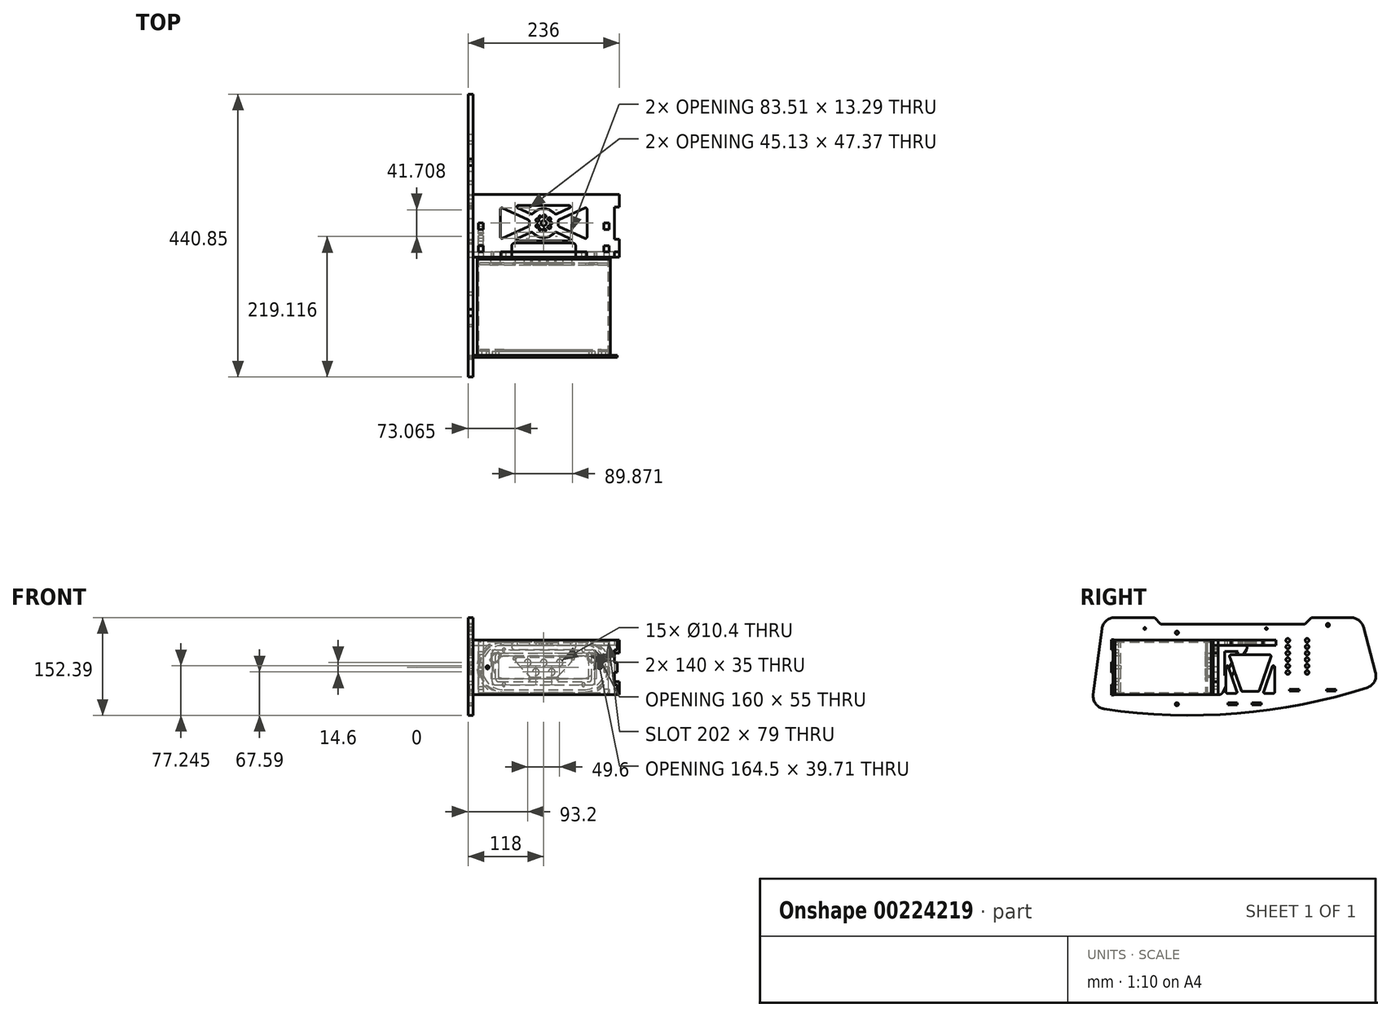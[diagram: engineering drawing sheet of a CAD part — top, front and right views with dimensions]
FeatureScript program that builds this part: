
annotation { "Feature Type Name" : "Feature", "Feature Type Description" : "" }
export const myFeature = defineFeature(function(context is Context, id is Id, definition is map)
    precondition{}
    {
        {
            var Q0;
            Q0=qCreatedBy(makeId("Front.planeOp"),FACE);
            var sketch = newSketch(context, id + "F0", { "sketchPlane" : qUnion([Q0])});
            skLineSegment(sketch, "E0.bottom", {"start": v(-61.5, 42.5) * mm, "end": v(61.5, 42.5) * mm});
            skLineSegment(sketch, "E0.top", {"start": v(-61.5, -42.5) * mm, "end": v(61.5, -42.5) * mm});
            skLineSegment(sketch, "E0.left", {"start": v(-61.5, 42.5) * mm, "end": v(-61.5, -42.5) * mm, "construction": true});
            skLineSegment(sketch, "E0.right", {"start": v(61.5, 42.5) * mm, "end": v(61.5, -42.5) * mm, "construction": true});
            skPoint(sketch, "E0.middle", {"position": v(0, 0) * mm});
            skArc(sketch, "E1", {"start": v(-61.5, 42.5) * mm, "mid": v(-104, 0) * mm, "end": v(-61.5, -42.5) * mm});
            skArc(sketch, "E2", {"start": v(61.5, -42.5) * mm, "mid": v(104, 0) * mm, "end": v(61.5, 42.5) * mm});
            skArc(sketch, "E3.0", {"start": v(61.5, -39.5) * mm, "mid": v(101, 0) * mm, "end": v(61.5, 39.5) * mm});
            skLineSegment(sketch, "E3.1", {"start": v(-61.5, -39.5) * mm, "end": v(61.5, -39.5) * mm});
            skArc(sketch, "E3.2", {"start": v(-61.5, 39.5) * mm, "mid": v(-101, 0) * mm, "end": v(-61.5, -39.5) * mm});
            skLineSegment(sketch, "E3.3", {"start": v(-61.5, 39.5) * mm, "end": v(61.5, 39.5) * mm});
            skSolve(sketch);
        }
        {
            var Q0;
            Q0=makeQuery(id+"F0.imprint","IMPRINT",FACE,{"disambiguationData":[TD([[makeQuery(id+"F0.imprint","IMPRINT",EDGE,{"derivedFrom":sQuery(id+"F0.wireOp",EDGE,"E0.bottom")}),-1.0]])]});
            extrude(context, id + "F1", {"entities" : qUnion([Q0]), "depth" : 150 * mm});
        }
        {
            var Q0;
            Q0=makeQuery(id+"F1.opExtrude","CAP_FACE",FACE,{"disambiguationData":[OSD([sQuery(id+"F0.wireOp",EDGE,"E0.bottom"),sQuery(id+"F0.wireOp",EDGE,"E0.top"),sQuery(id+"F0.wireOp",EDGE,"E1"),sQuery(id+"F0.wireOp",EDGE,"E2"),sQuery(id+"F0.wireOp",EDGE,"E3.0"),sQuery(id+"F0.wireOp",EDGE,"E3.1"),sQuery(id+"F0.wireOp",EDGE,"E3.2"),sQuery(id+"F0.wireOp",EDGE,"E3.3")])],"isStart":true});
            var sketch = newSketch(context, id + "F2", { "sketchPlane" : qUnion([Q0])});
            skArc(sketch, "E4.0", {"start": v(-61.5, -42.5) * mm, "mid": v(-104, 0) * mm, "end": v(-61.5, 42.5) * mm});
            skLineSegment(sketch, "E4.1", {"start": v(61.5, 42.5) * mm, "end": v(-61.5, 42.5) * mm});
            skArc(sketch, "E4.2", {"start": v(61.5, 42.5) * mm, "mid": v(104, 0) * mm, "end": v(61.5, -42.5) * mm});
            skLineSegment(sketch, "E4.3", {"start": v(61.5, -42.5) * mm, "end": v(-61.5, -42.5) * mm});
            skLineSegment(sketch, "E5", {"start": v(0, 23.45) * mm, "end": v(0, 0) * mm, "construction": true});
            skLineSegment(sketch, "E6", {"start": v(-31.44, 0) * mm, "end": v(0, 0) * mm, "construction": true});
            skCircle(sketch, "E7", {"center": v(-62, 27) * mm, "radius": 2.84 * mm});
            skCircle(sketch, "E8.MirrorC", {"center": v(62, 27) * mm, "radius": 2.84 * mm});
            skCircle(sketch, "E9.MirrorC", {"center": v(-62, -27) * mm, "radius": 2.84 * mm});
            skCircle(sketch, "E10.MirrorC", {"center": v(62, -27) * mm, "radius": 2.84 * mm});
            skCircle(sketch, "E11", {"center": v(-24.8, 7.3) * mm, "radius": 5.2 * mm});
            skLineSegment(sketch, "E12.bottom", {"start": v(-30, 12.5) * mm, "end": v(30, 12.5) * mm, "construction": true});
            skLineSegment(sketch, "E12.top", {"start": v(-30, -12.5) * mm, "end": v(30, -12.5) * mm, "construction": true});
            skLineSegment(sketch, "E12.left", {"start": v(-30, 12.5) * mm, "end": v(-30, -12.5) * mm, "construction": true});
            skLineSegment(sketch, "E12.right", {"start": v(30, 12.5) * mm, "end": v(30, -12.5) * mm, "construction": true});
            skPoint(sketch, "E12.middle", {"position": v(0, 0) * mm});
            skCircle(sketch, "E13", {"center": v(0, 7.3) * mm, "radius": 5.2 * mm});
            skCircle(sketch, "E14", {"center": v(24.8, 7.3) * mm, "radius": 5.2 * mm});
            skCircle(sketch, "E15", {"center": v(-12.4, -7.3) * mm, "radius": 5.2 * mm});
            skCircle(sketch, "E16", {"center": v(12.4, -7.3) * mm, "radius": 5.2 * mm});
            skLineSegment(sketch, "E17", {"start": v(-24.8, 7.3) * mm, "end": v(0, 7.3) * mm, "construction": true});
            skLineSegment(sketch, "E18", {"start": v(0, 7.3) * mm, "end": v(24.8, 7.3) * mm, "construction": true});
            skLineSegment(sketch, "E19", {"start": v(-12.4, -7.3) * mm, "end": v(-12.4, 7.3) * mm, "construction": true});
            skLineSegment(sketch, "E20", {"start": v(12.4, -7.3) * mm, "end": v(12.4, 7.3) * mm, "construction": true});
            skCircle(sketch, "E21", {"center": v(-75, 15) * mm, "radius": 7.25 * mm});
            skCircle(sketch, "E22.MirrorC", {"center": v(75, 15) * mm, "radius": 7.25 * mm});
            skSolve(sketch);
        }
        {
            var Q0;
            Q0=makeQuery(id+"F2.imprint","IMPRINT",FACE,{"disambiguationData":[TD([[makeQuery(id+"F2.imprint","IMPRINT",EDGE,{"derivedFrom":sQuery(id+"F2.wireOp",EDGE,"E7")}),-1.0]])]});
            var Q1;
            Q1=makeQuery(id+"F2.imprint","IMPRINT",FACE,{"disambiguationData":[TD([[makeQuery(id+"F2.imprint","IMPRINT",EDGE,{"derivedFrom":sQuery(id+"F2.wireOp",EDGE,"E4.0")}),-1.0]])]});
            extrude(context, id + "F3", {"entities" : qUnion([Q0, Q1]), "depth" : 3 * mm});
        }
        {
            var Q0;
            Q0=makeQuery(id+"F3.opExtrude","CAP_FACE",FACE,{"disambiguationData":[OSD([sQuery(id+"F2.wireOp",EDGE,"E4.0"),sQuery(id+"F2.wireOp",EDGE,"E4.1"),sQuery(id+"F2.wireOp",EDGE,"E4.2"),sQuery(id+"F2.wireOp",EDGE,"E4.3"),sQuery(id+"F2.wireOp",EDGE,"E7"),sQuery(id+"F2.wireOp",EDGE,"E8.MirrorC"),sQuery(id+"F2.wireOp",EDGE,"E9.MirrorC"),sQuery(id+"F2.wireOp",EDGE,"E10.MirrorC"),sQuery(id+"F2.wireOp",EDGE,"E11"),sQuery(id+"F2.wireOp",EDGE,"E13"),sQuery(id+"F2.wireOp",EDGE,"E14"),sQuery(id+"F2.wireOp",EDGE,"E15"),sQuery(id+"F2.wireOp",EDGE,"E16"),sQuery(id+"F2.wireOp",EDGE,"E21"),sQuery(id+"F2.wireOp",EDGE,"E22.MirrorC")])],"isStart":true});
            var sketch = newSketch(context, id + "F4", { "sketchPlane" : qUnion([Q0])});
            skCircle(sketch, "E23.0", {"center": v(-75, 15) * mm, "radius": 7.25 * mm});
            skCircle(sketch, "E23.1", {"center": v(-62, 27) * mm, "radius": 2.84 * mm});
            skCircle(sketch, "E23.2", {"center": v(-62, -27) * mm, "radius": 2.84 * mm});
            skCircle(sketch, "E23.3", {"center": v(62, -27) * mm, "radius": 2.84 * mm});
            skCircle(sketch, "E23.4", {"center": v(62, 27) * mm, "radius": 2.84 * mm});
            skCircle(sketch, "E23.5", {"center": v(75, 15) * mm, "radius": 7.25 * mm});
            skLineSegment(sketch, "E24.0", {"start": v(-61.5, 39.5) * mm, "end": v(61.5, 39.5) * mm});
            skArc(sketch, "E24.1", {"start": v(-61.5, 39.5) * mm, "mid": v(-101, 0) * mm, "end": v(-61.5, -39.5) * mm});
            skLineSegment(sketch, "E24.2", {"start": v(-61.5, -39.5) * mm, "end": v(61.5, -39.5) * mm});
            skArc(sketch, "E24.3", {"start": v(61.5, -39.5) * mm, "mid": v(101, 0) * mm, "end": v(61.5, 39.5) * mm});
            skArc(sketch, "E25.0", {"start": v(-61.5, 35.05) * mm, "mid": v(-96.55, 0) * mm, "end": v(-61.5, -35.05) * mm});
            skLineSegment(sketch, "E25.1", {"start": v(-61.5, 35.05) * mm, "end": v(61.5, 35.05) * mm});
            skArc(sketch, "E25.2", {"start": v(61.5, -35.05) * mm, "mid": v(96.55, 0) * mm, "end": v(61.5, 35.05) * mm});
            skLineSegment(sketch, "E25.3", {"start": v(-61.5, -35.05) * mm, "end": v(61.5, -35.05) * mm});
            skLineSegment(sketch, "E26", {"start": v(-46.82, 4.18) * mm, "end": v(-26.32, -17.82) * mm});
            skLineSegment(sketch, "E27", {"start": v(-19, -21) * mm, "end": v(19, -21) * mm});
            skLineSegment(sketch, "E28", {"start": v(26.32, -17.82) * mm, "end": v(46.82, 4.18) * mm});
            skLineSegment(sketch, "E29", {"start": v(39.5, 21) * mm, "end": v(-39.5, 21) * mm});
            skLineSegment(sketch, "E30", {"start": v(0, 21) * mm, "end": v(0, -21) * mm});
            skPoint(sketch, "E31.visualSharp", {"position": v(-62.49, 21) * mm});
            skArc(sketch, "E31.filletArc", {"start": v(-39.5, 21) * mm, "mid": v(-48.67, 14.99) * mm, "end": v(-46.82, 4.18) * mm});
            skPoint(sketch, "E32.visualSharp", {"position": v(-23.35, -21) * mm});
            skArc(sketch, "E32.filletArc", {"start": v(-26.32, -17.82) * mm, "mid": v(-22.99, -20.17) * mm, "end": v(-19, -21) * mm});
            skPoint(sketch, "E33.visualSharp", {"position": v(23.35, -21) * mm});
            skArc(sketch, "E33.filletArc", {"start": v(19, -21) * mm, "mid": v(22.99, -20.17) * mm, "end": v(26.32, -17.82) * mm});
            skPoint(sketch, "E34.visualSharp", {"position": v(62.49, 21) * mm});
            skArc(sketch, "E34.filletArc", {"start": v(46.82, 4.18) * mm, "mid": v(48.67, 14.99) * mm, "end": v(39.5, 21) * mm});
            skSolve(sketch);
        }
        {
            var Q0;
            Q0=makeQuery(id+"F4.imprint","IMPRINT",FACE,{"disambiguationData":[TD([[makeQuery(id+"F4.imprint","IMPRINT",EDGE,{"derivedFrom":sQuery(id+"F4.wireOp",EDGE,"E23.0")}),-1.0]])]});
            extrude(context, id + "F5", {"entities" : qUnion([Q0]), "depth" : 6 * mm});
        }
        {
            var Q0;
            Q0=makeQuery(id+"F3.opExtrude","CAP_FACE",FACE,{"disambiguationData":[OSD([sQuery(id+"F2.wireOp",EDGE,"E4.0"),sQuery(id+"F2.wireOp",EDGE,"E4.1"),sQuery(id+"F2.wireOp",EDGE,"E4.2"),sQuery(id+"F2.wireOp",EDGE,"E4.3"),sQuery(id+"F2.wireOp",EDGE,"E7"),sQuery(id+"F2.wireOp",EDGE,"E8.MirrorC"),sQuery(id+"F2.wireOp",EDGE,"E9.MirrorC"),sQuery(id+"F2.wireOp",EDGE,"E10.MirrorC"),sQuery(id+"F2.wireOp",EDGE,"E11"),sQuery(id+"F2.wireOp",EDGE,"E13"),sQuery(id+"F2.wireOp",EDGE,"E14"),sQuery(id+"F2.wireOp",EDGE,"E15"),sQuery(id+"F2.wireOp",EDGE,"E16"),sQuery(id+"F2.wireOp",EDGE,"E21"),sQuery(id+"F2.wireOp",EDGE,"E22.MirrorC")])],"isStart":true});
            var sketch = newSketch(context, id + "F6", { "sketchPlane" : qUnion([Q0])});
            skCircle(sketch, "E35.0", {"center": v(-24.8, 7.3) * mm, "radius": 5.2 * mm});
            skCircle(sketch, "E35.1", {"center": v(0, 7.3) * mm, "radius": 5.2 * mm});
            skCircle(sketch, "E35.2", {"center": v(24.8, 7.3) * mm, "radius": 5.2 * mm});
            skCircle(sketch, "E35.3", {"center": v(12.4, -7.3) * mm, "radius": 5.2 * mm});
            skCircle(sketch, "E35.4", {"center": v(-12.4, -7.3) * mm, "radius": 5.2 * mm});
            skLineSegment(sketch, "E36.0", {"start": v(39.5, 21) * mm, "end": v(-39.5, 21) * mm});
            skArc(sketch, "E36.1", {"start": v(-39.5, 21) * mm, "mid": v(-48.67, 14.99) * mm, "end": v(-46.82, 4.18) * mm});
            skLineSegment(sketch, "E36.2", {"start": v(-46.82, 4.18) * mm, "end": v(-26.32, -17.82) * mm});
            skArc(sketch, "E36.3", {"start": v(-26.32, -17.82) * mm, "mid": v(-22.99, -20.17) * mm, "end": v(-19, -21) * mm});
            skLineSegment(sketch, "E36.4", {"start": v(-19, -21) * mm, "end": v(19, -21) * mm});
            skArc(sketch, "E36.5", {"start": v(19, -21) * mm, "mid": v(22.99, -20.17) * mm, "end": v(26.32, -17.82) * mm});
            skLineSegment(sketch, "E36.6", {"start": v(26.32, -17.82) * mm, "end": v(46.82, 4.18) * mm});
            skArc(sketch, "E36.7", {"start": v(46.82, 4.18) * mm, "mid": v(48.67, 14.99) * mm, "end": v(39.5, 21) * mm});
            skLineSegment(sketch, "E37.0", {"start": v(39.5, 15.5) * mm, "end": v(-39.5, 15.5) * mm});
            skArc(sketch, "E37.1", {"start": v(42.8, 7.93) * mm, "mid": v(43.63, 12.8) * mm, "end": v(39.5, 15.5) * mm});
            skArc(sketch, "E37.2", {"start": v(-39.5, 15.5) * mm, "mid": v(-43.63, 12.8) * mm, "end": v(-42.8, 7.93) * mm});
            skLineSegment(sketch, "E37.3", {"start": v(22.3, -14.07) * mm, "end": v(42.8, 7.93) * mm});
            skLineSegment(sketch, "E37.4", {"start": v(-42.8, 7.93) * mm, "end": v(-22.3, -14.07) * mm});
            skArc(sketch, "E37.5", {"start": v(-22.3, -14.07) * mm, "mid": v(-20.8, -15.13) * mm, "end": v(-19, -15.5) * mm});
            skLineSegment(sketch, "E37.6", {"start": v(-19, -15.5) * mm, "end": v(19, -15.5) * mm});
            skArc(sketch, "E37.7", {"start": v(19, -15.5) * mm, "mid": v(20.8, -15.13) * mm, "end": v(22.3, -14.07) * mm});
            skSolve(sketch);
        }
        {
            var Q0;
            Q0=makeQuery(id+"F6.imprint","IMPRINT",FACE,{"disambiguationData":[TD([[makeQuery(id+"F6.imprint","IMPRINT",EDGE,{"derivedFrom":sQuery(id+"F6.wireOp",EDGE,"E35.0")}),1.0]])]});
            extrude(context, id + "F7", {"entities" : qUnion([Q0]), "depth" : 6 * mm});
        }
        {
            var Q0;
            Q0=makeQuery(id+"F5.opExtrude","CAP_FACE",FACE,{"disambiguationData":[OSD([sQuery(id+"F4.wireOp",EDGE,"E23.0"),sQuery(id+"F4.wireOp",EDGE,"E23.1"),sQuery(id+"F4.wireOp",EDGE,"E23.2"),sQuery(id+"F4.wireOp",EDGE,"E23.3"),sQuery(id+"F4.wireOp",EDGE,"E23.4"),sQuery(id+"F4.wireOp",EDGE,"E23.5"),sQuery(id+"F4.wireOp",EDGE,"E25.0"),sQuery(id+"F4.wireOp",EDGE,"E25.1"),sQuery(id+"F4.wireOp",EDGE,"E25.2"),sQuery(id+"F4.wireOp",EDGE,"E25.3"),sQuery(id+"F4.wireOp",EDGE,"E26"),sQuery(id+"F4.wireOp",EDGE,"E27"),sQuery(id+"F4.wireOp",EDGE,"E28"),sQuery(id+"F4.wireOp",EDGE,"E29"),sQuery(id+"F4.wireOp",EDGE,"E31.filletArc"),sQuery(id+"F4.wireOp",EDGE,"E32.filletArc"),sQuery(id+"F4.wireOp",EDGE,"E33.filletArc"),sQuery(id+"F4.wireOp",EDGE,"E34.filletArc")])],"isStart":false});
            var sketch = newSketch(context, id + "F8", { "sketchPlane" : qUnion([Q0])});
            skArc(sketch, "E38.0", {"start": v(-61.5, 38.5) * mm, "mid": v(-100, 0) * mm, "end": v(-61.5, -38.5) * mm});
            skLineSegment(sketch, "E38.1", {"start": v(-61.5, 38.5) * mm, "end": v(61.5, 38.5) * mm});
            skArc(sketch, "E38.2", {"start": v(61.5, -38.5) * mm, "mid": v(100, 0) * mm, "end": v(61.5, 38.5) * mm});
            skLineSegment(sketch, "E38.3", {"start": v(-61.5, -38.5) * mm, "end": v(61.5, -38.5) * mm});
            skCircle(sketch, "E39.0", {"center": v(-24.8, 7.3) * mm, "radius": 5.2 * mm});
            skCircle(sketch, "E39.1", {"center": v(0, 7.3) * mm, "radius": 5.2 * mm});
            skCircle(sketch, "E39.2", {"center": v(24.8, 7.3) * mm, "radius": 5.2 * mm});
            skCircle(sketch, "E39.3", {"center": v(12.4, -7.3) * mm, "radius": 5.2 * mm});
            skCircle(sketch, "E39.4", {"center": v(-12.4, -7.3) * mm, "radius": 5.2 * mm});
            skPoint(sketch, "E40", {"position": v(-75, 15) * mm});
            skLineSegment(sketch, "E41", {"start": v(-71.82, 25.25) * mm, "end": v(-85.25, 11.82) * mm});
            skLineSegment(sketch, "E42", {"start": v(-85.25, 11.82) * mm, "end": v(-78.18, 4.75) * mm});
            skLineSegment(sketch, "E43", {"start": v(-78.18, 4.75) * mm, "end": v(-64.75, 18.18) * mm});
            skLineSegment(sketch, "E44", {"start": v(-64.75, 18.18) * mm, "end": v(-71.82, 25.25) * mm});
            skLineSegment(sketch, "E45", {"start": v(-85.25, 11.82) * mm, "end": v(-85.25, 27.38) * mm});
            skLineSegment(sketch, "E46", {"start": v(-71.82, 25.25) * mm, "end": v(-78.18, 4.75) * mm, "construction": true});
            skCircle(sketch, "E47", {"center": v(-75, 15) * mm, "radius": 5.25 * mm});
            skLineSegment(sketch, "E48", {"start": v(-68.28, 21.72) * mm, "end": v(-81.72, 8.28) * mm, "construction": true});
            skLineSegment(sketch, "E49", {"start": v(-78.54, 18.54) * mm, "end": v(-71.46, 11.46) * mm, "construction": true});
            skLineSegment(sketch, "E50", {"start": v(-70.86, 24.3) * mm, "end": v(-78, 19.3) * mm});
            skLineSegment(sketch, "E51.MirrorCS", {"start": v(-65.7, 19.14) * mm, "end": v(-70.7, 12) * mm});
            skLineSegment(sketch, "E52.MirrorCS", {"start": v(-84.3, 10.86) * mm, "end": v(-79.3, 18) * mm});
            skLineSegment(sketch, "E53.MirrorCS", {"start": v(-79.14, 5.7) * mm, "end": v(-72, 10.7) * mm});
            skLineSegment(sketch, "E54", {"start": v(0, -1.17) * mm, "end": v(0, 25.72) * mm, "construction": true});
            skPoint(sketch, "E54.endSnap0", {"position": v(0, 21) * mm});
            skLineSegment(sketch, "E55.MirrorCS", {"start": v(78.54, 18.54) * mm, "end": v(71.46, 11.46) * mm, "construction": true});
            skLineSegment(sketch, "E56.MirrorCS", {"start": v(85.25, 11.82) * mm, "end": v(78.18, 4.75) * mm});
            skLineSegment(sketch, "E57.MirrorCS", {"start": v(64.75, 18.18) * mm, "end": v(71.82, 25.25) * mm});
            skArc(sketch, "E58.MirrorCS", {"start": v(61.5, 38.5) * mm, "mid": v(100, 0) * mm, "end": v(61.5, -38.5) * mm});
            skLineSegment(sketch, "E59.MirrorCS", {"start": v(84.3, 10.86) * mm, "end": v(79.3, 18) * mm});
            skCircle(sketch, "E60.MirrorC", {"center": v(75, 15) * mm, "radius": 5.25 * mm});
            skLineSegment(sketch, "E61.MirrorCS", {"start": v(71.82, 25.25) * mm, "end": v(78.18, 4.75) * mm, "construction": true});
            skLineSegment(sketch, "E62.MirrorCS", {"start": v(71.82, 25.25) * mm, "end": v(85.25, 11.82) * mm});
            skLineSegment(sketch, "E63.MirrorCS", {"start": v(70.86, 24.3) * mm, "end": v(78, 19.3) * mm});
            skLineSegment(sketch, "E64.MirrorCS", {"start": v(85.25, 11.82) * mm, "end": v(85.25, 27.38) * mm});
            skLineSegment(sketch, "E65.MirrorCS", {"start": v(68.28, 21.72) * mm, "end": v(81.72, 8.28) * mm, "construction": true});
            skLineSegment(sketch, "E66.MirrorCS", {"start": v(65.7, 19.14) * mm, "end": v(70.7, 12) * mm});
            skLineSegment(sketch, "E67.MirrorCS", {"start": v(79.14, 5.7) * mm, "end": v(72, 10.7) * mm});
            skLineSegment(sketch, "E68.MirrorCS", {"start": v(78.18, 4.75) * mm, "end": v(64.75, 18.18) * mm});
            skPoint(sketch, "E69", {"position": v(-48.67, 14.99) * mm});
            skPoint(sketch, "E70.0", {"position": v(-43.63, 12.8) * mm});
            skLineSegment(sketch, "E71", {"start": v(-48.67, 14.99) * mm, "end": v(-43.63, 12.8) * mm, "construction": true});
            skCircle(sketch, "E72", {"center": v(-46.15, 13.9) * mm, "radius": 2 * mm});
            skLineSegment(sketch, "E73", {"start": v(-22.99, -20.17) * mm, "end": v(-20.8, -15.13) * mm, "construction": true});
            skCircle(sketch, "E74", {"center": v(-21.9, -17.65) * mm, "radius": 2 * mm});
            skCircle(sketch, "E75.MirrorC", {"center": v(46.15, 13.9) * mm, "radius": 2 * mm});
            skCircle(sketch, "E76.MirrorC", {"center": v(21.9, -17.65) * mm, "radius": 2 * mm});
            skSolve(sketch);
        }
        {
            var Q0;
            Q0=makeQuery(id+"F8.imprint","IMPRINT",FACE,{"disambiguationData":[TD([[makeQuery(id+"F8.imprint","IMPRINT",EDGE,{"derivedFrom":makeQuery(id+"F5.opExtrude","CAP_EDGE",EDGE,{"disambiguationData":[OSD([sQuery(id+"F4.wireOp",EDGE,"E23.1")])],"isStart":false})}),1.0]])]});
            var Q1;
            Q1=makeQuery(id+"F8.imprint","IMPRINT",FACE,{"disambiguationData":[TD([[makeQuery(id+"F8.imprint","IMPRINT",EDGE,{"derivedFrom":makeQuery(id+"F5.opExtrude","CAP_EDGE",EDGE,{"disambiguationData":[OSD([sQuery(id+"F4.wireOp",EDGE,"E23.2")])],"isStart":false})}),-1.0]])]});
            var Q2;
            Q2=makeQuery(id+"F8.imprint","IMPRINT",FACE,{"disambiguationData":[TD([[makeQuery(id+"F8.imprint","IMPRINT",EDGE,{"derivedFrom":makeQuery(id+"F5.opExtrude","CAP_EDGE",EDGE,{"disambiguationData":[OSD([sQuery(id+"F4.wireOp",EDGE,"E23.3")])],"isStart":false})}),1.0]])]});
            var Q3;
            Q3=makeQuery(id+"F8.imprint","IMPRINT",FACE,{"disambiguationData":[TD([[makeQuery(id+"F8.imprint","IMPRINT",EDGE,{"derivedFrom":makeQuery(id+"F5.opExtrude","CAP_EDGE",EDGE,{"disambiguationData":[OSD([sQuery(id+"F4.wireOp",EDGE,"E23.4")])],"isStart":false})}),-1.0]])]});
            var Q4;
            Q4=makeQuery(id+"F8.imprint","IMPRINT",FACE,{"disambiguationData":[TD([[makeQuery(id+"F8.imprint","IMPRINT",EDGE,{"derivedFrom":sQuery(id+"F8.wireOp",EDGE,"E39.0")}),-1.0]])]});
            var Q5;
            {var subQ0=sQuery(id+"F8.wireOp",EDGE,"E50");var subQ3=sQuery(id+"F8.wireOp",EDGE,"E41");var subQ4=makeQuery(id+"F8.imprint","INTERSECT",VERTEX,{"derivedFrom":[subQ3,subQ0]});Q5=makeQuery(id+"F8.imprint","IMPRINT",FACE,{"disambiguationData":[TD([[makeQuery(id+"F8.imprint","IMPRINT",EDGE,{"disambiguationData":[TD([[subQ4,1.0]])],"derivedFrom":subQ3}),-1.0]])]});}
            var Q6;
            {var subQ1=sQuery(id+"F8.wireOp",EDGE,"E59.MirrorCS");var subQ8=sQuery(id+"F8.wireOp",EDGE,"E60.MirrorC");var subQ9=makeQuery(id+"F8.imprint","INTERSECT",VERTEX,{"derivedFrom":[subQ1,subQ8]});Q6=makeQuery(id+"F8.imprint","IMPRINT",FACE,{"disambiguationData":[TD([[makeQuery(id+"F8.imprint","IMPRINT",EDGE,{"disambiguationData":[TD([[subQ9,1.0]])],"derivedFrom":subQ1}),-1.0]])]});}
            var Q7;
            {var subQ5=sQuery(id+"F8.wireOp",EDGE,"E60.MirrorC");var subQ7=sQuery(id+"F8.wireOp",EDGE,"E66.MirrorCS");var subQ8=makeQuery(id+"F8.imprint","INTERSECT",VERTEX,{"derivedFrom":[subQ5,subQ7]});Q7=makeQuery(id+"F8.imprint","IMPRINT",FACE,{"disambiguationData":[TD([[makeQuery(id+"F8.imprint","IMPRINT",EDGE,{"disambiguationData":[TD([[subQ8,1.0]])],"derivedFrom":subQ5}),1.0]])]});}
            var Q8;
            Q8=makeQuery(id+"F8.imprint","IMPRINT",FACE,{"disambiguationData":[TD([[makeQuery(id+"F8.imprint","IMPRINT",EDGE,{"derivedFrom":sQuery(id+"F8.wireOp",EDGE,"E38.0")}),1.0]])]});
            var Q9;
            Q9=makeQuery(id+"F8.imprint","IMPRINT",FACE,{"disambiguationData":[TD([[makeQuery(id+"F8.imprint","IMPRINT",EDGE,{"derivedFrom":makeQuery(id+"F5.opExtrude","CAP_EDGE",EDGE,{"disambiguationData":[OSD([sQuery(id+"F4.wireOp",EDGE,"E23.1")])],"isStart":false})}),-1.0]])]});
            var Q10;
            {var subQ0=sQuery(id+"F8.wireOp",EDGE,"E43");var subQ1=sQuery(id+"F8.wireOp",EDGE,"E42");var subQ2=makeQuery(id+"F8.imprint","INTERSECT",VERTEX,{"derivedFrom":[subQ1,subQ0]});Q10=makeQuery(id+"F8.imprint","IMPRINT",FACE,{"disambiguationData":[TD([[makeQuery(id+"F8.imprint","IMPRINT",EDGE,{"disambiguationData":[TD([[subQ2,1.0]])],"derivedFrom":subQ1}),1.0]])]});}
            var Q11;
            {var subQ0=sQuery(id+"F8.wireOp",EDGE,"E53.MirrorCS");var subQ1=sQuery(id+"F8.wireOp",EDGE,"E43");var subQ2=makeQuery(id+"F8.imprint","INTERSECT",VERTEX,{"derivedFrom":[subQ1,subQ0]});Q11=makeQuery(id+"F8.imprint","IMPRINT",FACE,{"disambiguationData":[TD([[makeQuery(id+"F8.imprint","IMPRINT",EDGE,{"disambiguationData":[TD([[subQ2,1.0]])],"derivedFrom":subQ1}),1.0]])]});}
            var Q12;
            {var subQ3=sQuery(id+"F8.wireOp",EDGE,"E43");var subQ8=sQuery(id+"F8.wireOp",EDGE,"E53.MirrorCS");var subQ10=makeQuery(id+"F8.imprint","INTERSECT",VERTEX,{"derivedFrom":[subQ3,subQ8]});Q12=makeQuery(id+"F8.imprint","IMPRINT",FACE,{"disambiguationData":[TD([[makeQuery(id+"F8.imprint","IMPRINT",EDGE,{"disambiguationData":[TD([[subQ10,1.0]])],"derivedFrom":subQ3}),-1.0]])]});}
            var Q13;
            {var subQ0=sQuery(id+"F8.wireOp",EDGE,"E51.MirrorCS");var subQ1=sQuery(id+"F8.wireOp",EDGE,"E43");var subQ2=makeQuery(id+"F8.imprint","INTERSECT",VERTEX,{"derivedFrom":[subQ1,subQ0]});Q13=makeQuery(id+"F8.imprint","IMPRINT",FACE,{"disambiguationData":[TD([[makeQuery(id+"F8.imprint","IMPRINT",EDGE,{"disambiguationData":[TD([[subQ2,-1.0]])],"derivedFrom":subQ1}),1.0]])]});}
            var Q14;
            {var subQ0=sQuery(id+"F8.wireOp",EDGE,"E44");var subQ1=sQuery(id+"F8.wireOp",EDGE,"E43");var subQ2=makeQuery(id+"F8.imprint","INTERSECT",VERTEX,{"derivedFrom":[subQ1,subQ0]});Q14=makeQuery(id+"F8.imprint","IMPRINT",FACE,{"disambiguationData":[TD([[makeQuery(id+"F8.imprint","IMPRINT",EDGE,{"disambiguationData":[TD([[subQ2,1.0]])],"derivedFrom":subQ1}),1.0]])]});}
            var Q15;
            {var subQ0=sQuery(id+"F8.wireOp",EDGE,"E44");var subQ1=sQuery(id+"F8.wireOp",EDGE,"E41");var subQ2=makeQuery(id+"F8.imprint","INTERSECT",VERTEX,{"derivedFrom":[subQ1,subQ0]});Q15=makeQuery(id+"F8.imprint","IMPRINT",FACE,{"disambiguationData":[TD([[makeQuery(id+"F8.imprint","IMPRINT",EDGE,{"disambiguationData":[TD([[subQ2,-1.0]])],"derivedFrom":subQ1}),1.0]])]});}
            var Q16;
            {var subQ0=sQuery(id+"F8.wireOp",EDGE,"E50");var subQ1=sQuery(id+"F8.wireOp",EDGE,"E41");var subQ2=makeQuery(id+"F8.imprint","INTERSECT",VERTEX,{"derivedFrom":[subQ1,subQ0]});Q16=makeQuery(id+"F8.imprint","IMPRINT",FACE,{"disambiguationData":[TD([[makeQuery(id+"F8.imprint","IMPRINT",EDGE,{"disambiguationData":[TD([[subQ2,1.0]])],"derivedFrom":subQ1}),1.0]])]});}
            var Q17;
            {var subQ0=sQuery(id+"F8.wireOp",EDGE,"E52.MirrorCS");var subQ1=sQuery(id+"F8.wireOp",EDGE,"E41");var subQ2=makeQuery(id+"F8.imprint","INTERSECT",VERTEX,{"derivedFrom":[subQ1,subQ0]});Q17=makeQuery(id+"F8.imprint","IMPRINT",FACE,{"disambiguationData":[TD([[makeQuery(id+"F8.imprint","IMPRINT",EDGE,{"disambiguationData":[TD([[subQ2,-1.0]])],"derivedFrom":subQ1}),1.0]])]});}
            var Q18;
            {var subQ0=sQuery(id+"F8.wireOp",EDGE,"E42");var subQ1=sQuery(id+"F8.wireOp",EDGE,"E41");var subQ2=makeQuery(id+"F8.imprint","INTERSECT",VERTEX,{"derivedFrom":[subQ1,subQ0]});Q18=makeQuery(id+"F8.imprint","IMPRINT",FACE,{"disambiguationData":[TD([[makeQuery(id+"F8.imprint","IMPRINT",EDGE,{"disambiguationData":[TD([[subQ2,1.0]])],"derivedFrom":subQ1}),1.0]])]});}
            var Q19;
            {var subQ0=sQuery(id+"F8.wireOp",EDGE,"E68.MirrorCS");var subQ1=sQuery(id+"F8.wireOp",EDGE,"E57.MirrorCS");var subQ2=makeQuery(id+"F8.imprint","INTERSECT",VERTEX,{"derivedFrom":[subQ1,subQ0]});Q19=makeQuery(id+"F8.imprint","IMPRINT",FACE,{"disambiguationData":[TD([[makeQuery(id+"F8.imprint","IMPRINT",EDGE,{"disambiguationData":[TD([[subQ2,-1.0]])],"derivedFrom":subQ1}),-1.0]])]});}
            var Q20;
            {var subQ0=sQuery(id+"F8.wireOp",EDGE,"E68.MirrorCS");var subQ1=sQuery(id+"F8.wireOp",EDGE,"E66.MirrorCS");var subQ2=makeQuery(id+"F8.imprint","INTERSECT",VERTEX,{"derivedFrom":[subQ1,subQ0]});Q20=makeQuery(id+"F8.imprint","IMPRINT",FACE,{"disambiguationData":[TD([[makeQuery(id+"F8.imprint","IMPRINT",EDGE,{"disambiguationData":[TD([[subQ2,1.0]])],"derivedFrom":subQ1}),-1.0]])]});}
            var Q21;
            {var subQ0=sQuery(id+"F8.wireOp",EDGE,"E68.MirrorCS");var subQ1=sQuery(id+"F8.wireOp",EDGE,"E67.MirrorCS");var subQ2=makeQuery(id+"F8.imprint","INTERSECT",VERTEX,{"derivedFrom":[subQ1,subQ0]});Q21=makeQuery(id+"F8.imprint","IMPRINT",FACE,{"disambiguationData":[TD([[makeQuery(id+"F8.imprint","IMPRINT",EDGE,{"disambiguationData":[TD([[subQ2,1.0]])],"derivedFrom":subQ1}),1.0]])]});}
            var Q22;
            {var subQ0=sQuery(id+"F8.wireOp",EDGE,"E68.MirrorCS");var subQ1=sQuery(id+"F8.wireOp",EDGE,"E56.MirrorCS");var subQ2=makeQuery(id+"F8.imprint","INTERSECT",VERTEX,{"derivedFrom":[subQ1,subQ0]});Q22=makeQuery(id+"F8.imprint","IMPRINT",FACE,{"disambiguationData":[TD([[makeQuery(id+"F8.imprint","IMPRINT",EDGE,{"disambiguationData":[TD([[subQ2,1.0]])],"derivedFrom":subQ1}),-1.0]])]});}
            var Q23;
            {var subQ0=sQuery(id+"F8.wireOp",EDGE,"E62.MirrorCS");var subQ1=sQuery(id+"F8.wireOp",EDGE,"E57.MirrorCS");var subQ2=makeQuery(id+"F8.imprint","INTERSECT",VERTEX,{"derivedFrom":[subQ1,subQ0]});Q23=makeQuery(id+"F8.imprint","IMPRINT",FACE,{"disambiguationData":[TD([[makeQuery(id+"F8.imprint","IMPRINT",EDGE,{"disambiguationData":[TD([[subQ2,1.0]])],"derivedFrom":subQ1}),-1.0]])]});}
            var Q24;
            {var subQ0=sQuery(id+"F8.wireOp",EDGE,"E63.MirrorCS");var subQ1=sQuery(id+"F8.wireOp",EDGE,"E62.MirrorCS");var subQ2=makeQuery(id+"F8.imprint","INTERSECT",VERTEX,{"derivedFrom":[subQ1,subQ0]});Q24=makeQuery(id+"F8.imprint","IMPRINT",FACE,{"disambiguationData":[TD([[makeQuery(id+"F8.imprint","IMPRINT",EDGE,{"disambiguationData":[TD([[subQ2,1.0]])],"derivedFrom":subQ1}),-1.0]])]});}
            var Q25;
            {var subQ0=sQuery(id+"F8.wireOp",EDGE,"E62.MirrorCS");var subQ1=sQuery(id+"F8.wireOp",EDGE,"E59.MirrorCS");var subQ2=makeQuery(id+"F8.imprint","INTERSECT",VERTEX,{"derivedFrom":[subQ1,subQ0]});Q25=makeQuery(id+"F8.imprint","IMPRINT",FACE,{"disambiguationData":[TD([[makeQuery(id+"F8.imprint","IMPRINT",EDGE,{"disambiguationData":[TD([[subQ2,1.0]])],"derivedFrom":subQ1}),-1.0]])]});}
            var Q26;
            {var subQ0=sQuery(id+"F8.wireOp",EDGE,"E62.MirrorCS");var subQ1=sQuery(id+"F8.wireOp",EDGE,"E56.MirrorCS");var subQ2=makeQuery(id+"F8.imprint","INTERSECT",VERTEX,{"derivedFrom":[subQ1,subQ0]});Q26=makeQuery(id+"F8.imprint","IMPRINT",FACE,{"disambiguationData":[TD([[makeQuery(id+"F8.imprint","IMPRINT",EDGE,{"disambiguationData":[TD([[subQ2,-1.0]])],"derivedFrom":subQ1}),-1.0]])]});}
            extrude(context, id + "F9", {"entities" : qUnion([Q0, Q1, Q2, Q3, Q4, Q5, Q6, Q7, Q8, Q9, Q10, Q11, Q12, Q13, Q14, Q15, Q16, Q17, Q18, Q19, Q20, Q21, Q22, Q23, Q24, Q25, Q26]), "depth" : 3 * mm});
        }
        {
            var Q0;
            Q0=makeQuery(id+"F3.opExtrude","CAP_FACE",FACE,{"disambiguationData":[OSD([sQuery(id+"F2.wireOp",EDGE,"E4.0"),sQuery(id+"F2.wireOp",EDGE,"E4.1"),sQuery(id+"F2.wireOp",EDGE,"E4.2"),sQuery(id+"F2.wireOp",EDGE,"E4.3"),sQuery(id+"F2.wireOp",EDGE,"E7"),sQuery(id+"F2.wireOp",EDGE,"E8.MirrorC"),sQuery(id+"F2.wireOp",EDGE,"E9.MirrorC"),sQuery(id+"F2.wireOp",EDGE,"E10.MirrorC"),sQuery(id+"F2.wireOp",EDGE,"E11"),sQuery(id+"F2.wireOp",EDGE,"E13"),sQuery(id+"F2.wireOp",EDGE,"E14"),sQuery(id+"F2.wireOp",EDGE,"E15"),sQuery(id+"F2.wireOp",EDGE,"E16"),sQuery(id+"F2.wireOp",EDGE,"E21"),sQuery(id+"F2.wireOp",EDGE,"E22.MirrorC")])],"isStart":false});
            var sketch = newSketch(context, id + "F10", { "sketchPlane" : qUnion([Q0])});
            skLineSegment(sketch, "E77.bottom", {"start": v(110, 42.5) * mm, "end": v(-110, 42.5) * mm});
            skLineSegment(sketch, "E77.top", {"start": v(110, -42.5) * mm, "end": v(-110, -42.5) * mm});
            skLineSegment(sketch, "E77.left", {"start": v(110, 42.5) * mm, "end": v(110, -42.5) * mm});
            skLineSegment(sketch, "E77.right", {"start": v(-110, 42.5) * mm, "end": v(-110, -42.5) * mm});
            skPoint(sketch, "E77.middle", {"position": v(0, 0) * mm});
            skLineSegment(sketch, "E78", {"start": v(0, 0) * mm, "end": v(0, 33.26) * mm, "construction": true});
            skLineSegment(sketch, "E79.bottom", {"start": v(-110, 42.5) * mm, "end": v(-118, 42.5) * mm});
            skLineSegment(sketch, "E79.top", {"start": v(-110, 22.5) * mm, "end": v(-118, 22.5) * mm});
            skLineSegment(sketch, "E79.left", {"start": v(-110, 42.5) * mm, "end": v(-110, 22.5) * mm});
            skLineSegment(sketch, "E79.right", {"start": v(-118, 42.5) * mm, "end": v(-118, 22.5) * mm});
            skLineSegment(sketch, "E80.bottom", {"start": v(-110, -42.5) * mm, "end": v(-118, -42.5) * mm});
            skLineSegment(sketch, "E80.top", {"start": v(-110, -22.5) * mm, "end": v(-118, -22.5) * mm});
            skLineSegment(sketch, "E80.left", {"start": v(-110, -42.5) * mm, "end": v(-110, -22.5) * mm});
            skLineSegment(sketch, "E80.right", {"start": v(-118, -42.5) * mm, "end": v(-118, -22.5) * mm});
            skCircle(sketch, "E81.0", {"center": v(-62, 27) * mm, "radius": 2.84 * mm});
            skCircle(sketch, "E81.1", {"center": v(-62, -27) * mm, "radius": 2.84 * mm});
            skCircle(sketch, "E81.2", {"center": v(62, -27) * mm, "radius": 2.84 * mm});
            skCircle(sketch, "E81.3", {"center": v(62, 27) * mm, "radius": 2.84 * mm});
            skLineSegment(sketch, "E82.bottom", {"start": v(-102, -34.5) * mm, "end": v(-94, -34.5) * mm});
            skLineSegment(sketch, "E82.top", {"start": v(-102, -42.5) * mm, "end": v(-94, -42.5) * mm});
            skLineSegment(sketch, "E82.left", {"start": v(-102, -34.5) * mm, "end": v(-102, -42.5) * mm});
            skLineSegment(sketch, "E82.right", {"start": v(-94, -34.5) * mm, "end": v(-94, -42.5) * mm});
            skLineSegment(sketch, "E83.bottom", {"start": v(-102, 0.5) * mm, "end": v(-94, 0.5) * mm});
            skLineSegment(sketch, "E83.top", {"start": v(-102, -7.5) * mm, "end": v(-94, -7.5) * mm});
            skLineSegment(sketch, "E83.left", {"start": v(-102, 0.5) * mm, "end": v(-102, -7.5) * mm});
            skLineSegment(sketch, "E83.right", {"start": v(-94, 0.5) * mm, "end": v(-94, -7.5) * mm});
            skLineSegment(sketch, "E84.MirrorCS", {"start": v(94, -34.5) * mm, "end": v(94, -42.5) * mm});
            skLineSegment(sketch, "E85.MirrorCS", {"start": v(102, -42.5) * mm, "end": v(94, -42.5) * mm});
            skLineSegment(sketch, "E86.MirrorCS", {"start": v(102, -34.5) * mm, "end": v(102, -42.5) * mm});
            skLineSegment(sketch, "E87.MirrorCS", {"start": v(102, 0.5) * mm, "end": v(94, 0.5) * mm});
            skLineSegment(sketch, "E88.MirrorCS", {"start": v(94, 0.5) * mm, "end": v(94, -7.5) * mm});
            skLineSegment(sketch, "E89.MirrorCS", {"start": v(102, -7.5) * mm, "end": v(94, -7.5) * mm});
            skLineSegment(sketch, "E90.MirrorCS", {"start": v(102, 0.5) * mm, "end": v(102, -7.5) * mm});
            skLineSegment(sketch, "E91.MirrorCS", {"start": v(110, 42.5) * mm, "end": v(118, 42.5) * mm});
            skLineSegment(sketch, "E92.MirrorCS", {"start": v(118, 42.5) * mm, "end": v(118, 22.5) * mm});
            skLineSegment(sketch, "E93.MirrorCS", {"start": v(110, 22.5) * mm, "end": v(118, 22.5) * mm});
            skLineSegment(sketch, "E94.MirrorCS", {"start": v(110, -22.5) * mm, "end": v(118, -22.5) * mm});
            skLineSegment(sketch, "E95.MirrorCS", {"start": v(118, -42.5) * mm, "end": v(118, -22.5) * mm});
            skLineSegment(sketch, "E96.MirrorCS", {"start": v(110, -42.5) * mm, "end": v(118, -42.5) * mm});
            skArc(sketch, "E97.0", {"start": v(-61.5, -17.5) * mm, "mid": v(-75.4, -10.63) * mm, "end": v(-78.39, 4.6) * mm});
            skArc(sketch, "E98.0", {"start": v(61.5, 17.5) * mm, "mid": v(62.9, 17.44) * mm, "end": v(64.3, 17.27) * mm});
            skLineSegment(sketch, "E99", {"start": v(-61.5, 17.5) * mm, "end": v(61.5, 17.5) * mm});
            skLineSegment(sketch, "E100", {"start": v(-61.5, -17.5) * mm, "end": v(61.5, -17.5) * mm});
            skArc(sketch, "E101", {"start": v(-77.04, 8.04) * mm, "mid": v(-70.15, 9.61) * mm, "end": v(-67.87, 16.3) * mm, "construction": true});
            skArc(sketch, "E102", {"start": v(-69.14, 19.27) * mm, "mid": v(-79.85, 20.39) * mm, "end": v(-79.86, 9.62) * mm});
            skArc(sketch, "E103", {"start": v(-77.04, 8.04) * mm, "mid": v(-73.2, 13) * mm, "end": v(-67.87, 16.3) * mm, "construction": true});
            skArc(sketch, "E104", {"start": v(-64.3, 17.27) * mm, "mid": v(-62.9, 17.44) * mm, "end": v(-61.5, 17.5) * mm});
            skArc(sketch, "E105", {"start": v(79.86, 9.62) * mm, "mid": v(79.85, 20.39) * mm, "end": v(69.14, 19.27) * mm});
            skLineSegment(sketch, "E106", {"start": v(67.87, 16.3) * mm, "end": v(67.87, 16.3) * mm});
            skLineSegment(sketch, "E107", {"start": v(77.04, 8.04) * mm, "end": v(77.04, 8.04) * mm});
            skArc(sketch, "E108", {"start": v(67.87, 16.3) * mm, "mid": v(70.15, 9.61) * mm, "end": v(77.04, 8.04) * mm, "construction": true});
            skArc(sketch, "E109", {"start": v(67.87, 16.3) * mm, "mid": v(73.2, 13) * mm, "end": v(77.04, 8.04) * mm, "construction": true});
            skArc(sketch, "E110", {"start": v(78.39, 4.6) * mm, "mid": v(75.4, -10.63) * mm, "end": v(61.5, -17.5) * mm});
            skPoint(sketch, "E111.visualSharp", {"position": v(-77.04, 8.04) * mm});
            skArc(sketch, "E111.filletArc", {"start": v(-78.39, 4.6) * mm, "mid": v(-78.41, 7.32) * mm, "end": v(-79.86, 9.62) * mm});
            skPoint(sketch, "E112.visualSharp", {"position": v(-67.87, 16.3) * mm});
            skArc(sketch, "E112.filletArc", {"start": v(-69.14, 19.27) * mm, "mid": v(-67, 17.59) * mm, "end": v(-64.3, 17.27) * mm});
            skPoint(sketch, "E113.visualSharp", {"position": v(67.87, 16.3) * mm});
            skArc(sketch, "E113.filletArc", {"start": v(64.3, 17.27) * mm, "mid": v(67, 17.59) * mm, "end": v(69.14, 19.27) * mm});
            skPoint(sketch, "E114.visualSharp", {"position": v(77.04, 8.04) * mm});
            skArc(sketch, "E114.filletArc", {"start": v(79.86, 9.62) * mm, "mid": v(78.41, 7.32) * mm, "end": v(78.39, 4.6) * mm});
            skLineSegment(sketch, "E115", {"start": v(102, -34.5) * mm, "end": v(94, -34.5) * mm});
            skLineSegment(sketch, "E116", {"start": v(61.5, 17.5) * mm, "end": v(61.5, -17.5) * mm, "construction": true});
            skLineSegment(sketch, "E117.bottom", {"start": v(-118, 42.5) * mm, "end": v(-67, 42.5) * mm});
            skLineSegment(sketch, "E117.top", {"start": v(-118, 34.5) * mm, "end": v(-67, 34.5) * mm});
            skLineSegment(sketch, "E117.left", {"start": v(-118, 42.5) * mm, "end": v(-118, 34.5) * mm});
            skLineSegment(sketch, "E117.right", {"start": v(-67, 42.5) * mm, "end": v(-67, 34.5) * mm});
            skLineSegment(sketch, "E118.bottom", {"start": v(-50, 42.5) * mm, "end": v(50, 42.5) * mm});
            skLineSegment(sketch, "E118.top", {"start": v(-45, 27.5) * mm, "end": v(45, 27.5) * mm});
            skLineSegment(sketch, "E118.left", {"start": v(-50, 42.5) * mm, "end": v(-50, 32.5) * mm});
            skLineSegment(sketch, "E118.right", {"start": v(50, 42.5) * mm, "end": v(50, 32.5) * mm});
            skPoint(sketch, "E118.middle", {"position": v(0, 35) * mm});
            skLineSegment(sketch, "E119.MirrorCS", {"start": v(67, 42.5) * mm, "end": v(67, 34.5) * mm});
            skLineSegment(sketch, "E120.MirrorCS", {"start": v(118, 34.5) * mm, "end": v(67, 34.5) * mm});
            skPoint(sketch, "E121.visualSharp", {"position": v(-50, 27.5) * mm});
            skArc(sketch, "E121.filletArc", {"start": v(-50, 32.5) * mm, "mid": v(-48.54, 28.96) * mm, "end": v(-45, 27.5) * mm});
            skPoint(sketch, "E122.visualSharp", {"position": v(50, 27.5) * mm});
            skArc(sketch, "E122.filletArc", {"start": v(45, 27.5) * mm, "mid": v(48.54, 28.96) * mm, "end": v(50, 32.5) * mm});
            skSolve(sketch);
        }
        {
            var Q0;
            {var subQ2=sQuery(id+"F10.wireOp",EDGE,"E94.MirrorCS");Q0=makeQuery(id+"F10.imprint","IMPRINT",FACE,{"disambiguationData":[TD([[makeQuery(id+"F10.imprint","IMPRINT",EDGE,{"derivedFrom":subQ2}),-1.0]])]});}
            var Q1;
            Q1=makeQuery(id+"F10.imprint","IMPRINT",FACE,{"disambiguationData":[TD([[makeQuery(id+"F10.imprint","IMPRINT",EDGE,{"derivedFrom":sQuery(id+"F10.wireOp",EDGE,"E79.bottom")}),1.0]])]});
            var Q2;
            Q2=makeQuery(id+"F10.imprint","IMPRINT",FACE,{"disambiguationData":[TD([[makeQuery(id+"F10.imprint","IMPRINT",EDGE,{"derivedFrom":sQuery(id+"F10.wireOp",EDGE,"E80.bottom")}),-1.0]])]});
            var Q3;
            {var subQ0=sQuery(id+"F10.wireOp",EDGE,"E77.bottom");var subQ1=makeQuery(id+"F3.opExtrude","CAP_EDGE",EDGE,{"disambiguationData":[OSD([sQuery(id+"F2.wireOp",EDGE,"E4.2")])],"isStart":false});var subQ2=makeQuery(id+"F10.imprint","INTERSECT",VERTEX,{"derivedFrom":[subQ1,subQ0]});Q3=makeQuery(id+"F10.imprint","IMPRINT",FACE,{"disambiguationData":[TD([[makeQuery(id+"F10.imprint","IMPRINT",EDGE,{"disambiguationData":[TD([[subQ2,1.0]])],"derivedFrom":subQ0}),1.0]])]});}
            var Q4;
            {var subQ0=sQuery(id+"F10.wireOp",EDGE,"E77.bottom");var subQ1=makeQuery(id+"F3.opExtrude","CAP_EDGE",EDGE,{"disambiguationData":[OSD([sQuery(id+"F2.wireOp",EDGE,"E4.0")])],"isStart":false});var subQ2=makeQuery(id+"F10.imprint","INTERSECT",VERTEX,{"derivedFrom":[subQ1,subQ0]});Q4=makeQuery(id+"F10.imprint","IMPRINT",FACE,{"disambiguationData":[TD([[makeQuery(id+"F10.imprint","IMPRINT",EDGE,{"disambiguationData":[TD([[subQ2,1.0]])],"derivedFrom":subQ1}),1.0]])]});}
            var Q5;
            {var subQ7=sQuery(id+"F10.wireOp",EDGE,"E86.MirrorCS");Q5=makeQuery(id+"F10.imprint","IMPRINT",FACE,{"disambiguationData":[TD([[makeQuery(id+"F10.imprint","IMPRINT",EDGE,{"derivedFrom":subQ7}),1.0]])]});}
            var Q6;
            Q6=makeQuery(id+"F10.imprint","IMPRINT",FACE,{"disambiguationData":[TD([[makeQuery(id+"F10.imprint","IMPRINT",EDGE,{"derivedFrom":sQuery(id+"F10.wireOp",EDGE,"E77.right")}),1.0]])]});
            var Q7;
            Q7=makeQuery(id+"F10.imprint","IMPRINT",FACE,{"disambiguationData":[TD([[makeQuery(id+"F10.imprint","IMPRINT",EDGE,{"derivedFrom":sQuery(id+"F10.wireOp",EDGE,"E81.0")}),-1.0]])]});
            var Q8;
            {var subQ0=sQuery(id+"F10.wireOp",EDGE,"E93.MirrorCS");Q8=makeQuery(id+"F10.imprint","IMPRINT",FACE,{"disambiguationData":[TD([[makeQuery(id+"F10.imprint","IMPRINT",EDGE,{"derivedFrom":subQ0}),1.0]])]});}
            var Q9;
            {var subQ0=sQuery(id+"F10.wireOp",EDGE,"E79.top");Q9=makeQuery(id+"F10.imprint","IMPRINT",FACE,{"disambiguationData":[TD([[makeQuery(id+"F10.imprint","IMPRINT",EDGE,{"derivedFrom":subQ0}),-1.0]])]});}
            extrude(context, id + "F11", {"entities" : qUnion([Q0, Q1, Q2, Q3, Q4, Q5, Q6, Q7, Q8, Q9]), "depth" : 8 * mm});
        }
        {
            var Q0;
            Q0=makeQuery(id+"F11.opExtrude","SWEPT_FACE",FACE,{"disambiguationData":[OSD([sQuery(id+"F10.wireOp",EDGE,"E120.MirrorCS")])]});
            var sketch = newSketch(context, id + "F12", { "sketchPlane" : qUnion([Q0])});
            skLineSegment(sketch, "E123.bottom", {"start": v(-118, 3) * mm, "end": v(-67, 3) * mm});
            skLineSegment(sketch, "E123.top", {"start": v(-118, 11) * mm, "end": v(-67, 11) * mm});
            skLineSegment(sketch, "E123.left", {"start": v(-118, 3) * mm, "end": v(-118, 11) * mm});
            skLineSegment(sketch, "E123.right", {"start": v(-67, 3) * mm, "end": v(-67, 11) * mm});
            skLineSegment(sketch, "E124.bottom", {"start": v(118, 3) * mm, "end": v(67, 3) * mm});
            skLineSegment(sketch, "E124.top", {"start": v(118, 11) * mm, "end": v(67, 11) * mm});
            skLineSegment(sketch, "E124.left", {"start": v(118, 3) * mm, "end": v(118, 11) * mm});
            skLineSegment(sketch, "E124.right", {"start": v(67, 3) * mm, "end": v(67, 11) * mm});
            skLineSegment(sketch, "E125.bottom", {"start": v(-118, 11) * mm, "end": v(118, 11) * mm});
            skLineSegment(sketch, "E125.top", {"start": v(-118, 101) * mm, "end": v(118, 101) * mm});
            skLineSegment(sketch, "E125.left", {"start": v(-118, 11) * mm, "end": v(-118, 101) * mm});
            skLineSegment(sketch, "E125.right", {"start": v(118, 11) * mm, "end": v(118, 101) * mm});
            skPoint(sketch, "E125.middle", {"position": v(0, 56) * mm});
            skLineSegment(sketch, "E126.bottom", {"start": v(-45, 25) * mm, "end": v(45, 25) * mm});
            skLineSegment(sketch, "E126.top", {"start": v(-50, 11) * mm, "end": v(50, 11) * mm});
            skLineSegment(sketch, "E126.left", {"start": v(-50, 20) * mm, "end": v(-50, 11) * mm});
            skLineSegment(sketch, "E126.right", {"start": v(50, 20) * mm, "end": v(50, 11) * mm});
            skLineSegment(sketch, "E127.bottom", {"start": v(-118, 81) * mm, "end": v(-110, 81) * mm});
            skLineSegment(sketch, "E127.top", {"start": v(-118, 31) * mm, "end": v(-110, 31) * mm});
            skLineSegment(sketch, "E127.left", {"start": v(-118, 81) * mm, "end": v(-118, 31) * mm});
            skLineSegment(sketch, "E127.right", {"start": v(-110, 81) * mm, "end": v(-110, 31) * mm});
            skPoint(sketch, "E127.middle", {"position": v(-114, 56) * mm});
            skLineSegment(sketch, "E128.bottom", {"start": v(118, 81) * mm, "end": v(110, 81) * mm});
            skLineSegment(sketch, "E128.top", {"start": v(118, 31) * mm, "end": v(110, 31) * mm});
            skLineSegment(sketch, "E128.left", {"start": v(118, 81) * mm, "end": v(118, 31) * mm});
            skLineSegment(sketch, "E128.right", {"start": v(110, 81) * mm, "end": v(110, 31) * mm});
            skPoint(sketch, "E128.middle", {"position": v(114, 56) * mm});
            skPoint(sketch, "E129.visualSharp", {"position": v(-50, 25) * mm});
            skArc(sketch, "E129.filletArc", {"start": v(-45, 25) * mm, "mid": v(-48.54, 23.54) * mm, "end": v(-50, 20) * mm});
            skPoint(sketch, "E130.visualSharp", {"position": v(50, 25) * mm});
            skArc(sketch, "E130.filletArc", {"start": v(50, 20) * mm, "mid": v(48.54, 23.54) * mm, "end": v(45, 25) * mm});
            skCircle(sketch, "E131", {"center": v(0, 56) * mm, "radius": 10.85 * mm, "construction": true});
            skCircle(sketch, "E132", {"center": v(0, 56) * mm, "radius": 11.55 * mm, "construction": true});
            skCircle(sketch, "E133", {"center": v(11.55, 56) * mm, "radius": 1.55 * mm});
            skCircle(sketch, "E134.1.0", {"center": v(-5.77, 66) * mm, "radius": 1.55 * mm});
            skCircle(sketch, "E134.2.0", {"center": v(-5.77, 46) * mm, "radius": 1.55 * mm});
            skLineSegment(sketch, "E135", {"start": v(0, 56) * mm, "end": v(11.55, 56) * mm, "construction": true});
            skLineSegment(sketch, "E136", {"start": v(0, 56) * mm, "end": v(5.77, 66) * mm, "construction": true});
            skCircle(sketch, "E137", {"center": v(1.04, 66.8) * mm, "radius": 2.5 * mm});
            skCircle(sketch, "E138", {"center": v(8.83, 62.3) * mm, "radius": 2.5 * mm});
            skLineSegment(sketch, "E139", {"start": v(1.04, 66.8) * mm, "end": v(8.83, 62.3) * mm, "construction": true});
            skCircle(sketch, "E140.1.0", {"center": v(-9.87, 60.5) * mm, "radius": 2.5 * mm});
            skCircle(sketch, "E140.1.1", {"center": v(-9.87, 51.5) * mm, "radius": 2.5 * mm});
            skCircle(sketch, "E140.2.0", {"center": v(1.04, 45.2) * mm, "radius": 2.5 * mm});
            skCircle(sketch, "E140.2.1", {"center": v(8.83, 49.7) * mm, "radius": 2.5 * mm});
            skCircle(sketch, "E141", {"center": v(0, 56) * mm, "radius": 4.15 * mm});
            skSolve(sketch);
        }
        {
            var Q0;
            Q0=makeQuery(id+"F12.imprint","IMPRINT",FACE,{"disambiguationData":[TD([[makeQuery(id+"F12.imprint","IMPRINT",EDGE,{"derivedFrom":sQuery(id+"F12.wireOp",EDGE,"E123.bottom")}),1.0]])]});
            var Q1;
            Q1=makeQuery(id+"F12.imprint","IMPRINT",FACE,{"disambiguationData":[TD([[makeQuery(id+"F12.imprint","IMPRINT",EDGE,{"derivedFrom":sQuery(id+"F12.wireOp",EDGE,"E124.bottom")}),-1.0]])]});
            var Q2;
            {var subQ1=sQuery(id+"F12.wireOp",EDGE,"E125.top");Q2=makeQuery(id+"F12.imprint","IMPRINT",FACE,{"disambiguationData":[TD([[makeQuery(id+"F12.imprint","IMPRINT",EDGE,{"derivedFrom":subQ1}),-1.0]])]});}
            extrude(context, id + "F13", {"entities" : qUnion([Q0, Q1, Q2]), "depth" : 8 * mm});
        }
        {
            var Q0;
            Q0=makeQuery(id+"F13.opExtrude","CAP_FACE",FACE,{"disambiguationData":[OSD([sQuery(id+"F12.wireOp",EDGE,"E123.bottom"),sQuery(id+"F12.wireOp",EDGE,"E123.left"),sQuery(id+"F12.wireOp",EDGE,"E123.right"),sQuery(id+"F12.wireOp",EDGE,"E124.bottom"),sQuery(id+"F12.wireOp",EDGE,"E124.left"),sQuery(id+"F12.wireOp",EDGE,"E124.right"),sQuery(id+"F12.wireOp",EDGE,"E125.bottom"),sQuery(id+"F12.wireOp",EDGE,"E125.top"),sQuery(id+"F12.wireOp",EDGE,"E125.left"),sQuery(id+"F12.wireOp",EDGE,"E125.right"),sQuery(id+"F12.wireOp",EDGE,"E126.bottom"),sQuery(id+"F12.wireOp",EDGE,"E126.left"),sQuery(id+"F12.wireOp",EDGE,"E126.right"),sQuery(id+"F12.wireOp",EDGE,"E127.bottom"),sQuery(id+"F12.wireOp",EDGE,"E127.top"),sQuery(id+"F12.wireOp",EDGE,"E127.right"),sQuery(id+"F12.wireOp",EDGE,"E128.bottom"),sQuery(id+"F12.wireOp",EDGE,"E128.top"),sQuery(id+"F12.wireOp",EDGE,"E128.right"),sQuery(id+"F12.wireOp",EDGE,"E129.filletArc"),sQuery(id+"F12.wireOp",EDGE,"E130.filletArc"),sQuery(id+"F12.wireOp",EDGE,"E133"),sQuery(id+"F12.wireOp",EDGE,"E134.1.0"),sQuery(id+"F12.wireOp",EDGE,"E134.2.0"),sQuery(id+"F12.wireOp",EDGE,"E137"),sQuery(id+"F12.wireOp",EDGE,"E138"),sQuery(id+"F12.wireOp",EDGE,"E140.1.0"),sQuery(id+"F12.wireOp",EDGE,"E140.1.1"),sQuery(id+"F12.wireOp",EDGE,"E140.2.0"),sQuery(id+"F12.wireOp",EDGE,"E140.2.1"),sQuery(id+"F12.wireOp",EDGE,"E141")])],"isStart":true});
            var sketch = newSketch(context, id + "F14", { "sketchPlane" : qUnion([Q0])});
            skLineSegment(sketch, "E142.bottom", {"start": v(72.5, -23.5) * mm, "end": v(-72.5, -23.5) * mm, "construction": true});
            skLineSegment(sketch, "E142.top", {"start": v(72.5, -88.5) * mm, "end": v(-72.5, -88.5) * mm, "construction": true});
            skLineSegment(sketch, "E142.left", {"start": v(72.5, -23.5) * mm, "end": v(72.5, -88.5) * mm, "construction": true});
            skLineSegment(sketch, "E142.right", {"start": v(-72.5, -23.5) * mm, "end": v(-72.5, -88.5) * mm, "construction": true});
            skPoint(sketch, "E142.middle", {"position": v(0, -56) * mm});
            skLineSegment(sketch, "E143", {"start": v(-72.5, -23.5) * mm, "end": v(-15.97, -48.84) * mm, "construction": true});
            skLineSegment(sketch, "E144", {"start": v(72.5, -23.5) * mm, "end": v(15.97, -48.84) * mm, "construction": true});
            skArc(sketch, "E145", {"start": v(-15.97, -48.84) * mm, "mid": v(-17.5, -56) * mm, "end": v(-15.97, -63.16) * mm, "construction": true});
            skLineSegment(sketch, "E146", {"start": v(15.97, -48.84) * mm, "end": v(15.97, -48.84) * mm});
            skLineSegment(sketch, "E147", {"start": v(15.97, -63.16) * mm, "end": v(72.5, -88.5) * mm, "construction": true});
            skArc(sketch, "E148", {"start": v(-15.97, -63.16) * mm, "mid": v(0, -73.5) * mm, "end": v(15.97, -63.16) * mm, "construction": true});
            skArc(sketch, "E149", {"start": v(15.97, -63.16) * mm, "mid": v(17.5, -56) * mm, "end": v(15.97, -48.84) * mm, "construction": true});
            skLineSegment(sketch, "E150", {"start": v(0, -56) * mm, "end": v(-15.97, -63.16) * mm, "construction": true});
            skLineSegment(sketch, "E151", {"start": v(-15.97, -48.84) * mm, "end": v(0, -56) * mm, "construction": true});
            skLineSegment(sketch, "E152", {"start": v(15.97, -63.16) * mm, "end": v(15.97, -63.16) * mm});
            skArc(sketch, "E153", {"start": v(15.97, -48.84) * mm, "mid": v(0, -38.5) * mm, "end": v(-15.97, -48.84) * mm, "construction": true});
            skLineSegment(sketch, "E154", {"start": v(-15.97, -63.16) * mm, "end": v(-72.5, -88.5) * mm, "construction": true});
            skLineSegment(sketch, "E155", {"start": v(15.97, -48.84) * mm, "end": v(0, -56) * mm, "construction": true});
            skLineSegment(sketch, "E156", {"start": v(0, -56) * mm, "end": v(15.97, -63.16) * mm, "construction": true});
            skLineSegment(sketch, "E157.0", {"start": v(39.77, -28.5) * mm, "end": v(-39.77, -28.5) * mm});
            skLineSegment(sketch, "E157.1", {"start": v(40.6, -32.33) * mm, "end": v(20.05, -41.53) * mm});
            skArc(sketch, "E157.2", {"start": v(16.6, -40.82) * mm, "mid": v(0, -33.5) * mm, "end": v(-16.6, -40.82) * mm});
            skLineSegment(sketch, "E157.3", {"start": v(-40.6, -32.33) * mm, "end": v(-20.05, -41.53) * mm});
            skLineSegment(sketch, "E158.0", {"start": v(-64.68, -32.48) * mm, "end": v(-24.14, -50.66) * mm});
            skLineSegment(sketch, "E158.1", {"start": v(-67.5, -34.3) * mm, "end": v(-67.5, -77.7) * mm});
            skLineSegment(sketch, "E158.2", {"start": v(-24.14, -61.34) * mm, "end": v(-64.68, -79.52) * mm});
            skArc(sketch, "E158.3", {"start": v(-22.38, -53.7) * mm, "mid": v(-22.5, -56) * mm, "end": v(-22.38, -58.3) * mm});
            skLineSegment(sketch, "E159.0", {"start": v(-20.05, -70.47) * mm, "end": v(-40.6, -79.67) * mm});
            skArc(sketch, "E159.1", {"start": v(-16.6, -71.18) * mm, "mid": v(0, -78.5) * mm, "end": v(16.6, -71.18) * mm});
            skLineSegment(sketch, "E159.2", {"start": v(20.05, -70.47) * mm, "end": v(40.6, -79.67) * mm});
            skLineSegment(sketch, "E159.3", {"start": v(39.77, -83.5) * mm, "end": v(-39.77, -83.5) * mm});
            skLineSegment(sketch, "E160.0", {"start": v(64.68, -32.48) * mm, "end": v(24.14, -50.66) * mm});
            skLineSegment(sketch, "E160.1", {"start": v(67.5, -34.3) * mm, "end": v(67.5, -77.7) * mm});
            skLineSegment(sketch, "E160.2", {"start": v(24.14, -61.34) * mm, "end": v(64.68, -79.52) * mm});
            skArc(sketch, "E160.3", {"start": v(22.38, -58.3) * mm, "mid": v(22.5, -56) * mm, "end": v(22.38, -53.7) * mm});
            skPoint(sketch, "E161.visualSharp", {"position": v(-49.12, -28.5) * mm});
            skArc(sketch, "E161.filletArc", {"start": v(-39.77, -28.5) * mm, "mid": v(-41.73, -30.08) * mm, "end": v(-40.6, -32.33) * mm});
            skPoint(sketch, "E162.visualSharp", {"position": v(49.12, -28.5) * mm});
            skArc(sketch, "E162.filletArc", {"start": v(40.6, -32.33) * mm, "mid": v(41.73, -30.08) * mm, "end": v(39.77, -28.5) * mm});
            skPoint(sketch, "E163.visualSharp", {"position": v(67.5, -31.22) * mm});
            skArc(sketch, "E163.filletArc", {"start": v(67.5, -34.3) * mm, "mid": v(66.59, -32.63) * mm, "end": v(64.68, -32.48) * mm});
            skPoint(sketch, "E164.visualSharp", {"position": v(67.5, -80.78) * mm});
            skArc(sketch, "E164.filletArc", {"start": v(64.68, -79.52) * mm, "mid": v(66.59, -79.37) * mm, "end": v(67.5, -77.7) * mm});
            skPoint(sketch, "E165.visualSharp", {"position": v(49.12, -83.5) * mm});
            skArc(sketch, "E165.filletArc", {"start": v(39.77, -83.5) * mm, "mid": v(41.73, -81.92) * mm, "end": v(40.6, -79.67) * mm});
            skPoint(sketch, "E166.visualSharp", {"position": v(-49.12, -83.5) * mm});
            skArc(sketch, "E166.filletArc", {"start": v(-40.6, -79.67) * mm, "mid": v(-41.73, -81.92) * mm, "end": v(-39.77, -83.5) * mm});
            skPoint(sketch, "E167.visualSharp", {"position": v(-67.5, -80.78) * mm});
            skArc(sketch, "E167.filletArc", {"start": v(-67.5, -77.7) * mm, "mid": v(-66.59, -79.37) * mm, "end": v(-64.68, -79.52) * mm});
            skPoint(sketch, "E168.visualSharp", {"position": v(-67.5, -31.22) * mm});
            skArc(sketch, "E168.filletArc", {"start": v(-64.68, -32.48) * mm, "mid": v(-66.59, -32.63) * mm, "end": v(-67.5, -34.3) * mm});
            skPoint(sketch, "E169.visualSharp", {"position": v(-17.97, -42.46) * mm});
            skArc(sketch, "E169.filletArc", {"start": v(-20.05, -41.53) * mm, "mid": v(-18.21, -41.73) * mm, "end": v(-16.6, -40.82) * mm});
            skPoint(sketch, "E170.visualSharp", {"position": v(17.97, -42.46) * mm});
            skArc(sketch, "E170.filletArc", {"start": v(16.6, -40.82) * mm, "mid": v(18.21, -41.73) * mm, "end": v(20.05, -41.53) * mm});
            skPoint(sketch, "E171.visualSharp", {"position": v(22.06, -51.59) * mm});
            skArc(sketch, "E171.filletArc", {"start": v(24.14, -50.66) * mm, "mid": v(22.77, -51.9) * mm, "end": v(22.38, -53.7) * mm});
            skPoint(sketch, "E172.visualSharp", {"position": v(22.06, -60.41) * mm});
            skArc(sketch, "E172.filletArc", {"start": v(22.38, -58.3) * mm, "mid": v(22.77, -60.1) * mm, "end": v(24.14, -61.34) * mm});
            skPoint(sketch, "E173.visualSharp", {"position": v(17.97, -69.54) * mm});
            skArc(sketch, "E173.filletArc", {"start": v(20.05, -70.47) * mm, "mid": v(18.21, -70.27) * mm, "end": v(16.6, -71.18) * mm});
            skPoint(sketch, "E174.visualSharp", {"position": v(-17.97, -69.54) * mm});
            skArc(sketch, "E174.filletArc", {"start": v(-16.6, -71.18) * mm, "mid": v(-18.21, -70.27) * mm, "end": v(-20.05, -70.47) * mm});
            skPoint(sketch, "E175.visualSharp", {"position": v(-22.06, -51.59) * mm});
            skArc(sketch, "E175.filletArc", {"start": v(-22.38, -53.7) * mm, "mid": v(-22.77, -51.9) * mm, "end": v(-24.14, -50.66) * mm});
            skPoint(sketch, "E176.visualSharp", {"position": v(-22.06, -60.41) * mm});
            skArc(sketch, "E176.filletArc", {"start": v(-24.14, -61.34) * mm, "mid": v(-22.77, -60.1) * mm, "end": v(-22.38, -58.3) * mm});
            skLineSegment(sketch, "E177.bottom", {"start": v(-102, -11) * mm, "end": v(-94, -11) * mm});
            skLineSegment(sketch, "E177.top", {"start": v(-102, -21) * mm, "end": v(-94, -21) * mm});
            skLineSegment(sketch, "E177.left", {"start": v(-102, -11) * mm, "end": v(-102, -21) * mm});
            skLineSegment(sketch, "E177.right", {"start": v(-94, -11) * mm, "end": v(-94, -21) * mm});
            skLineSegment(sketch, "E178.bottom", {"start": v(-102, -46) * mm, "end": v(-94, -46) * mm});
            skLineSegment(sketch, "E178.top", {"start": v(-102, -56) * mm, "end": v(-94, -56) * mm});
            skLineSegment(sketch, "E178.left", {"start": v(-102, -46) * mm, "end": v(-102, -56) * mm});
            skLineSegment(sketch, "E178.right", {"start": v(-94, -46) * mm, "end": v(-94, -56) * mm});
            skLineSegment(sketch, "E179", {"start": v(0, -56) * mm, "end": v(0, -112.5) * mm, "construction": true});
            skPoint(sketch, "E179.endSnap0", {"position": v(0, -101) * mm});
            skLineSegment(sketch, "E180.MirrorCS", {"start": v(102, -21) * mm, "end": v(94, -21) * mm});
            skLineSegment(sketch, "E181.MirrorCS", {"start": v(102, -46) * mm, "end": v(94, -46) * mm});
            skLineSegment(sketch, "E182.MirrorCS", {"start": v(102, -56) * mm, "end": v(94, -56) * mm});
            skLineSegment(sketch, "E183.MirrorCS", {"start": v(102, -11) * mm, "end": v(94, -11) * mm});
            skLineSegment(sketch, "E184.MirrorCS", {"start": v(94, -46) * mm, "end": v(94, -56) * mm});
            skLineSegment(sketch, "E185.MirrorCS", {"start": v(94, -11) * mm, "end": v(94, -21) * mm});
            skLineSegment(sketch, "E186.MirrorCS", {"start": v(102, -11) * mm, "end": v(102, -21) * mm});
            skLineSegment(sketch, "E187.MirrorCS", {"start": v(102, -46) * mm, "end": v(102, -56) * mm});
            skSolve(sketch);
        }
        {
            var Q0;
            Q0=makeQuery(id+"F14.imprint","IMPRINT",FACE,{"disambiguationData":[TD([[makeQuery(id+"F14.imprint","IMPRINT",EDGE,{"derivedFrom":sQuery(id+"F14.wireOp",EDGE,"E157.0")}),1.0]])]});
            var Q1;
            Q1=makeQuery(id+"F14.imprint","IMPRINT",FACE,{"disambiguationData":[TD([[makeQuery(id+"F14.imprint","IMPRINT",EDGE,{"derivedFrom":sQuery(id+"F14.wireOp",EDGE,"E158.0")}),-1.0]])]});
            var Q2;
            Q2=makeQuery(id+"F14.imprint","IMPRINT",FACE,{"disambiguationData":[TD([[makeQuery(id+"F14.imprint","IMPRINT",EDGE,{"derivedFrom":sQuery(id+"F14.wireOp",EDGE,"E159.0")}),1.0]])]});
            var Q3;
            Q3=makeQuery(id+"F14.imprint","IMPRINT",FACE,{"disambiguationData":[TD([[makeQuery(id+"F14.imprint","IMPRINT",EDGE,{"derivedFrom":sQuery(id+"F14.wireOp",EDGE,"E160.0")}),1.0]])]});
            var Q4;
            Q4=makeQuery(id+"F14.imprint","IMPRINT",FACE,{"disambiguationData":[TD([[makeQuery(id+"F14.imprint","IMPRINT",EDGE,{"derivedFrom":sQuery(id+"F14.wireOp",EDGE,"E177.bottom")}),-1.0]])]});
            var Q5;
            Q5=makeQuery(id+"F14.imprint","IMPRINT",FACE,{"disambiguationData":[TD([[makeQuery(id+"F14.imprint","IMPRINT",EDGE,{"derivedFrom":sQuery(id+"F14.wireOp",EDGE,"E178.bottom")}),-1.0]])]});
            var Q6;
            Q6=makeQuery(id+"F14.imprint","IMPRINT",FACE,{"disambiguationData":[TD([[makeQuery(id+"F14.imprint","IMPRINT",EDGE,{"derivedFrom":sQuery(id+"F14.wireOp",EDGE,"E180.MirrorCS")}),-1.0]])]});
            var Q7;
            Q7=makeQuery(id+"F14.imprint","IMPRINT",FACE,{"disambiguationData":[TD([[makeQuery(id+"F14.imprint","IMPRINT",EDGE,{"derivedFrom":sQuery(id+"F14.wireOp",EDGE,"E181.MirrorCS")}),1.0]])]});
            extrude(context, id + "F15", {"entities" : qUnion([Q0, Q1, Q2, Q3, Q4, Q5, Q6, Q7]), "operationType" : NewBodyOperationType.REMOVE, "oppositeDirection" : true, "depth" : 25 * mm});
        }
        {
            var Q0;
            Q0=makeQuery(id+"F15.boolean.opBoolean","COPY",FACE,{"derivedFrom":makeQuery(id+"F15.opExtrude","SWEPT_FACE",FACE,{"disambiguationData":[OSD([sQuery(id+"F14.wireOp",EDGE,"E177.right")])]})});
            var sketch = newSketch(context, id + "F16", { "sketchPlane" : qUnion([Q0])});
            skLineSegment(sketch, "E188", {"start": v(-12.47, -42.5) * mm, "end": v(-3, -42.5) * mm});
            skLineSegment(sketch, "E189", {"start": v(-3, -42.5) * mm, "end": v(-3, -34.5) * mm});
            skLineSegment(sketch, "E190", {"start": v(-3, -34.5) * mm, "end": v(-11, -34.5) * mm});
            skLineSegment(sketch, "E191", {"start": v(-11, -34.5) * mm, "end": v(-11, -7.5) * mm});
            skLineSegment(sketch, "E192", {"start": v(-11, -7.5) * mm, "end": v(-3, -7.5) * mm});
            skLineSegment(sketch, "E193", {"start": v(-3, -7.5) * mm, "end": v(-3, 0.5) * mm});
            skLineSegment(sketch, "E194", {"start": v(-3, 0.5) * mm, "end": v(-11, 0.5) * mm});
            skLineSegment(sketch, "E195", {"start": v(-11, 0.5) * mm, "end": v(-11, 42.5) * mm});
            skLineSegment(sketch, "E196", {"start": v(-11, 42.5) * mm, "end": v(-21, 42.5) * mm});
            skLineSegment(sketch, "E197", {"start": v(-21, 42.5) * mm, "end": v(-21, 34.5) * mm});
            skLineSegment(sketch, "E198", {"start": v(-21, 34.5) * mm, "end": v(-46, 34.5) * mm});
            skLineSegment(sketch, "E199", {"start": v(-46, 34.5) * mm, "end": v(-46, 42.5) * mm});
            skLineSegment(sketch, "E200", {"start": v(-46, 42.5) * mm, "end": v(-56, 42.5) * mm});
            skLineSegment(sketch, "E201", {"start": v(-56, 42.5) * mm, "end": v(-56, 31.05) * mm});
            skLineSegment(sketch, "E202", {"start": v(-55.24, 28.14) * mm, "end": v(-17.71, -39.41) * mm});
            skPoint(sketch, "E203.visualSharp", {"position": v(-16, -42.5) * mm});
            skArc(sketch, "E203.filletArc", {"start": v(-17.71, -39.41) * mm, "mid": v(-15.51, -41.67) * mm, "end": v(-12.47, -42.5) * mm});
            skPoint(sketch, "E204.visualSharp", {"position": v(-56, 29.5) * mm});
            skArc(sketch, "E204.filletArc", {"start": v(-56, 31.05) * mm, "mid": v(-55.8, 29.55) * mm, "end": v(-55.24, 28.14) * mm});
            skLineSegment(sketch, "E205", {"start": v(-21, -12.9) * mm, "end": v(-21, 24.5) * mm});
            skLineSegment(sketch, "E206", {"start": v(-21, 24.5) * mm, "end": v(-41.78, 24.5) * mm});
            skLineSegment(sketch, "E207", {"start": v(-41.78, 24.5) * mm, "end": v(-21, -12.9) * mm});
            skSolve(sketch);
        }
        {
            var Q0;
            Q0 = qSketchRegion(id + "F16", true);
            extrude(context, id + "F17", {"entities" : qUnion([Q0]), "depth" : 8 * mm});
        }
        {
            var Q0;
            Q0=makeQuery(id+"F1.opExtrude","CAP_FACE",FACE,{"disambiguationData":[OSD([sQuery(id+"F0.wireOp",EDGE,"E0.bottom"),sQuery(id+"F0.wireOp",EDGE,"E0.top"),sQuery(id+"F0.wireOp",EDGE,"E1"),sQuery(id+"F0.wireOp",EDGE,"E2"),sQuery(id+"F0.wireOp",EDGE,"E3.0"),sQuery(id+"F0.wireOp",EDGE,"E3.1"),sQuery(id+"F0.wireOp",EDGE,"E3.2"),sQuery(id+"F0.wireOp",EDGE,"E3.3")])],"isStart":false});
            var sketch = newSketch(context, id + "F18", { "sketchPlane" : qUnion([Q0])});
            skLineSegment(sketch, "E208.bottom", {"start": v(110, -42.5) * mm, "end": v(-110, -42.5) * mm});
            skLineSegment(sketch, "E208.top", {"start": v(110, 42.5) * mm, "end": v(-110, 42.5) * mm});
            skLineSegment(sketch, "E208.left", {"start": v(110, -42.5) * mm, "end": v(110, 42.5) * mm});
            skLineSegment(sketch, "E208.right", {"start": v(-110, -42.5) * mm, "end": v(-110, 42.5) * mm});
            skPoint(sketch, "E208.middle", {"position": v(0, 0) * mm});
            skLineSegment(sketch, "E209.bottom", {"start": v(110, -42.5) * mm, "end": v(115, -42.5) * mm});
            skLineSegment(sketch, "E209.top", {"start": v(110, -27.5) * mm, "end": v(115, -27.5) * mm});
            skLineSegment(sketch, "E209.left", {"start": v(110, -42.5) * mm, "end": v(110, -27.5) * mm});
            skLineSegment(sketch, "E209.right", {"start": v(115, -42.5) * mm, "end": v(115, -27.5) * mm});
            skLineSegment(sketch, "E210.bottom", {"start": v(110, 42.5) * mm, "end": v(115, 42.5) * mm});
            skLineSegment(sketch, "E210.top", {"start": v(110, 27.5) * mm, "end": v(115, 27.5) * mm});
            skLineSegment(sketch, "E210.left", {"start": v(110, 42.5) * mm, "end": v(110, 27.5) * mm});
            skLineSegment(sketch, "E210.right", {"start": v(115, 42.5) * mm, "end": v(115, 27.5) * mm});
            skLineSegment(sketch, "E211.bottom", {"start": v(110, -7.5) * mm, "end": v(115, -7.5) * mm});
            skLineSegment(sketch, "E211.top", {"start": v(110, 7.5) * mm, "end": v(115, 7.5) * mm});
            skLineSegment(sketch, "E211.left", {"start": v(110, -7.5) * mm, "end": v(110, 7.5) * mm});
            skLineSegment(sketch, "E211.right", {"start": v(115, -7.5) * mm, "end": v(115, 7.5) * mm});
            skPoint(sketch, "E211.middle", {"position": v(112.5, 0) * mm});
            skLineSegment(sketch, "E212", {"start": v(0, 0) * mm, "end": v(0, -30.62) * mm, "construction": true});
            skLineSegment(sketch, "E213.MirrorCS", {"start": v(-110, -42.5) * mm, "end": v(-115, -42.5) * mm});
            skLineSegment(sketch, "E214.MirrorCS", {"start": v(-115, -42.5) * mm, "end": v(-115, -27.5) * mm});
            skLineSegment(sketch, "E215.MirrorCS", {"start": v(-110, -27.5) * mm, "end": v(-115, -27.5) * mm});
            skLineSegment(sketch, "E216.MirrorCS", {"start": v(-110, -7.5) * mm, "end": v(-115, -7.5) * mm});
            skLineSegment(sketch, "E217.MirrorCS", {"start": v(-115, -7.5) * mm, "end": v(-115, 7.5) * mm});
            skLineSegment(sketch, "E218.MirrorCS", {"start": v(-110, 7.5) * mm, "end": v(-115, 7.5) * mm});
            skLineSegment(sketch, "E219.MirrorCS", {"start": v(-110, 27.5) * mm, "end": v(-115, 27.5) * mm});
            skLineSegment(sketch, "E220.MirrorCS", {"start": v(-115, 42.5) * mm, "end": v(-115, 27.5) * mm});
            skLineSegment(sketch, "E221.MirrorCS", {"start": v(-110, 42.5) * mm, "end": v(-115, 42.5) * mm});
            skCircle(sketch, "E222", {"center": v(87.5, 0) * mm, "radius": 2.5 * mm});
            skCircle(sketch, "E223.MirrorC", {"center": v(-87.5, 0) * mm, "radius": 2.5 * mm});
            skSolve(sketch);
        }
        {
            var Q0;
            Q0 = qSketchRegion(id + "F18", true);
            extrude(context, id + "F19", {"entities" : qUnion([Q0]), "depth" : 3 * mm});
        }
        {
            var Q0;
            Q0=makeQuery(id+"F19.opExtrude","CAP_FACE",FACE,{"disambiguationData":[OSD([sQuery(id+"F18.wireOp",EDGE,"E208.bottom"),sQuery(id+"F18.wireOp",EDGE,"E208.top"),sQuery(id+"F18.wireOp",EDGE,"E208.left"),sQuery(id+"F18.wireOp",EDGE,"E208.right"),sQuery(id+"F18.wireOp",EDGE,"E209.bottom"),sQuery(id+"F18.wireOp",EDGE,"E209.top"),sQuery(id+"F18.wireOp",EDGE,"E209.right"),sQuery(id+"F18.wireOp",EDGE,"E210.bottom"),sQuery(id+"F18.wireOp",EDGE,"E210.top"),sQuery(id+"F18.wireOp",EDGE,"E210.right"),sQuery(id+"F18.wireOp",EDGE,"E211.bottom"),sQuery(id+"F18.wireOp",EDGE,"E211.top"),sQuery(id+"F18.wireOp",EDGE,"E211.right"),sQuery(id+"F18.wireOp",EDGE,"E213.MirrorCS"),sQuery(id+"F18.wireOp",EDGE,"E214.MirrorCS"),sQuery(id+"F18.wireOp",EDGE,"E215.MirrorCS"),sQuery(id+"F18.wireOp",EDGE,"E216.MirrorCS"),sQuery(id+"F18.wireOp",EDGE,"E217.MirrorCS"),sQuery(id+"F18.wireOp",EDGE,"E218.MirrorCS"),sQuery(id+"F18.wireOp",EDGE,"E219.MirrorCS"),sQuery(id+"F18.wireOp",EDGE,"E220.MirrorCS"),sQuery(id+"F18.wireOp",EDGE,"E221.MirrorCS"),sQuery(id+"F18.wireOp",EDGE,"E222"),sQuery(id+"F18.wireOp",EDGE,"E223.MirrorC")])],"isStart":true});
            var sketch = newSketch(context, id + "F20", { "sketchPlane" : qUnion([Q0])});
            skArc(sketch, "E224.0", {"start": v(61.5, 35.05) * mm, "mid": v(96.55, 0) * mm, "end": v(61.5, -35.05) * mm});
            skLineSegment(sketch, "E224.1", {"start": v(61.5, -35.05) * mm, "end": v(-61.5, -35.05) * mm});
            skArc(sketch, "E224.2", {"start": v(-61.5, -35.05) * mm, "mid": v(-96.55, 0) * mm, "end": v(-61.5, 35.05) * mm});
            skLineSegment(sketch, "E224.3", {"start": v(61.5, 35.05) * mm, "end": v(-61.5, 35.05) * mm});
            skCircle(sketch, "E225.0", {"center": v(87.5, 0) * mm, "radius": 2.5 * mm});
            skCircle(sketch, "E225.1", {"center": v(-87.5, 0) * mm, "radius": 2.5 * mm});
            skLineSegment(sketch, "E226.bottom", {"start": v(75, -27.5) * mm, "end": v(-75, -27.5) * mm});
            skLineSegment(sketch, "E226.top", {"start": v(75, 27.5) * mm, "end": v(-75, 27.5) * mm});
            skLineSegment(sketch, "E226.left", {"start": v(80, -22.5) * mm, "end": v(80, 22.5) * mm});
            skLineSegment(sketch, "E226.right", {"start": v(-80, -22.5) * mm, "end": v(-80, 22.5) * mm});
            skPoint(sketch, "E226.middle", {"position": v(0, 0) * mm});
            skPoint(sketch, "E227.visualSharp", {"position": v(80, -27.5) * mm});
            skArc(sketch, "E227.filletArc", {"start": v(75, -27.5) * mm, "mid": v(78.54, -26.04) * mm, "end": v(80, -22.5) * mm});
            skPoint(sketch, "E228.visualSharp", {"position": v(80, 27.5) * mm});
            skArc(sketch, "E228.filletArc", {"start": v(80, 22.5) * mm, "mid": v(78.54, 26.04) * mm, "end": v(75, 27.5) * mm});
            skPoint(sketch, "E229.visualSharp", {"position": v(-80, 27.5) * mm});
            skArc(sketch, "E229.filletArc", {"start": v(-75, 27.5) * mm, "mid": v(-78.54, 26.04) * mm, "end": v(-80, 22.5) * mm});
            skPoint(sketch, "E230.visualSharp", {"position": v(-80, -27.5) * mm});
            skArc(sketch, "E230.filletArc", {"start": v(-80, -22.5) * mm, "mid": v(-78.54, -26.04) * mm, "end": v(-75, -27.5) * mm});
            skSolve(sketch);
        }
        {
            var Q0;
            Q0 = qSketchRegion(id + "F20", true);
            extrude(context, id + "F21", {"entities" : qUnion([Q0]), "depth" : 6 * mm});
        }
        {
            var Q0;
            Q0=makeQuery(id+"F19.opExtrude","CAP_FACE",FACE,{"disambiguationData":[OSD([sQuery(id+"F18.wireOp",EDGE,"E208.bottom"),sQuery(id+"F18.wireOp",EDGE,"E208.top"),sQuery(id+"F18.wireOp",EDGE,"E208.left"),sQuery(id+"F18.wireOp",EDGE,"E208.right"),sQuery(id+"F18.wireOp",EDGE,"E209.bottom"),sQuery(id+"F18.wireOp",EDGE,"E209.top"),sQuery(id+"F18.wireOp",EDGE,"E209.right"),sQuery(id+"F18.wireOp",EDGE,"E210.bottom"),sQuery(id+"F18.wireOp",EDGE,"E210.top"),sQuery(id+"F18.wireOp",EDGE,"E210.right"),sQuery(id+"F18.wireOp",EDGE,"E211.bottom"),sQuery(id+"F18.wireOp",EDGE,"E211.top"),sQuery(id+"F18.wireOp",EDGE,"E211.right"),sQuery(id+"F18.wireOp",EDGE,"E213.MirrorCS"),sQuery(id+"F18.wireOp",EDGE,"E214.MirrorCS"),sQuery(id+"F18.wireOp",EDGE,"E215.MirrorCS"),sQuery(id+"F18.wireOp",EDGE,"E216.MirrorCS"),sQuery(id+"F18.wireOp",EDGE,"E217.MirrorCS"),sQuery(id+"F18.wireOp",EDGE,"E218.MirrorCS"),sQuery(id+"F18.wireOp",EDGE,"E219.MirrorCS"),sQuery(id+"F18.wireOp",EDGE,"E220.MirrorCS"),sQuery(id+"F18.wireOp",EDGE,"E221.MirrorCS"),sQuery(id+"F18.wireOp",EDGE,"E222"),sQuery(id+"F18.wireOp",EDGE,"E223.MirrorC")])],"isStart":true});
            var sketch = newSketch(context, id + "F22", { "sketchPlane" : qUnion([Q0])});
            skLineSegment(sketch, "E231.bottom", {"start": v(70, -22.5) * mm, "end": v(-70, -22.5) * mm});
            skLineSegment(sketch, "E231.top", {"start": v(70, 22.5) * mm, "end": v(-70, 22.5) * mm});
            skLineSegment(sketch, "E231.left", {"start": v(75, -17.5) * mm, "end": v(75, 17.5) * mm});
            skLineSegment(sketch, "E231.right", {"start": v(-75, -17.5) * mm, "end": v(-75, 17.5) * mm});
            skPoint(sketch, "E231.middle", {"position": v(0, 0) * mm});
            skLineSegment(sketch, "E232.0", {"start": v(70, -17.5) * mm, "end": v(-70, -17.5) * mm});
            skLineSegment(sketch, "E232.1", {"start": v(70, -17.5) * mm, "end": v(70, 17.5) * mm});
            skLineSegment(sketch, "E232.2", {"start": v(70, 17.5) * mm, "end": v(-70, 17.5) * mm});
            skLineSegment(sketch, "E232.3", {"start": v(-70, -17.5) * mm, "end": v(-70, 17.5) * mm});
            skPoint(sketch, "E233.visualSharp", {"position": v(75, -22.5) * mm});
            skArc(sketch, "E233.filletArc", {"start": v(70, -22.5) * mm, "mid": v(73.54, -21.04) * mm, "end": v(75, -17.5) * mm});
            skPoint(sketch, "E234.visualSharp", {"position": v(75, 22.5) * mm});
            skArc(sketch, "E234.filletArc", {"start": v(75, 17.5) * mm, "mid": v(73.54, 21.04) * mm, "end": v(70, 22.5) * mm});
            skPoint(sketch, "E235.visualSharp", {"position": v(-75, 22.5) * mm});
            skArc(sketch, "E235.filletArc", {"start": v(-70, 22.5) * mm, "mid": v(-73.54, 21.04) * mm, "end": v(-75, 17.5) * mm});
            skPoint(sketch, "E236.visualSharp", {"position": v(-75, -22.5) * mm});
            skArc(sketch, "E236.filletArc", {"start": v(-75, -17.5) * mm, "mid": v(-73.54, -21.04) * mm, "end": v(-70, -22.5) * mm});
            skSolve(sketch);
        }
        {
            var Q0;
            Q0 = qSketchRegion(id + "F22", true);
            extrude(context, id + "F23", {"entities" : qUnion([Q0]), "depth" : 6 * mm});
        }
        {
            var Q0;
            Q0=makeQuery(id+"F23.opExtrude","CAP_FACE",FACE,{"disambiguationData":[OSD([sQuery(id+"F22.wireOp",EDGE,"E231.bottom"),sQuery(id+"F22.wireOp",EDGE,"E231.top"),sQuery(id+"F22.wireOp",EDGE,"E231.left"),sQuery(id+"F22.wireOp",EDGE,"E231.right"),sQuery(id+"F22.wireOp",EDGE,"E232.0"),sQuery(id+"F22.wireOp",EDGE,"E232.1"),sQuery(id+"F22.wireOp",EDGE,"E232.2"),sQuery(id+"F22.wireOp",EDGE,"E232.3"),sQuery(id+"F22.wireOp",EDGE,"E233.filletArc"),sQuery(id+"F22.wireOp",EDGE,"E234.filletArc"),sQuery(id+"F22.wireOp",EDGE,"E235.filletArc"),sQuery(id+"F22.wireOp",EDGE,"E236.filletArc")])],"isStart":false});
            var sketch = newSketch(context, id + "F24", { "sketchPlane" : qUnion([Q0])});
            skArc(sketch, "E237.0", {"start": v(61.5, 38.5) * mm, "mid": v(100, 0) * mm, "end": v(61.5, -38.5) * mm});
            skLineSegment(sketch, "E237.1", {"start": v(61.5, -38.5) * mm, "end": v(-61.5, -38.5) * mm});
            skLineSegment(sketch, "E237.2", {"start": v(61.5, 38.5) * mm, "end": v(-61.5, 38.5) * mm});
            skArc(sketch, "E237.3", {"start": v(-61.5, 38.5) * mm, "mid": v(-100, 0) * mm, "end": v(-61.5, -38.5) * mm});
            skLineSegment(sketch, "E238.0", {"start": v(70, -17.5) * mm, "end": v(70, 17.5) * mm});
            skLineSegment(sketch, "E238.1", {"start": v(70, -17.5) * mm, "end": v(-70, -17.5) * mm});
            skLineSegment(sketch, "E238.2", {"start": v(70, 17.5) * mm, "end": v(-70, 17.5) * mm});
            skLineSegment(sketch, "E238.3", {"start": v(-70, -17.5) * mm, "end": v(-70, 17.5) * mm});
            skCircle(sketch, "E239.0", {"center": v(87.5, 0) * mm, "radius": 2.5 * mm});
            skCircle(sketch, "E239.1", {"center": v(-87.5, 0) * mm, "radius": 2.5 * mm});
            skSolve(sketch);
        }
        {
            var Q0;
            Q0 = qSketchRegion(id + "F24", true);
            extrude(context, id + "F25", {"entities" : qUnion([Q0]), "depth" : 3 * mm});
        }
        {
            var Q0;
            Q0=makeQuery(id+"F13.opExtrude","SWEPT_FACE",FACE,{"disambiguationData":[OSD([sQuery(id+"F12.wireOp",EDGE,"E127.right")])]});
            var sketch = newSketch(context, id + "F26", { "sketchPlane" : qUnion([Q0])});
            skLineSegment(sketch, "E240", {"start": v(183.8, -42.5) * mm, "end": v(170.29, 60.11) * mm});
            skLineSegment(sketch, "E241", {"start": v(150.46, 77.5) * mm, "end": v(88.46, 77.5) * mm});
            skLineSegment(sketch, "E242", {"start": v(88.46, 77.5) * mm, "end": v(78.46, 67.5) * mm});
            skLineSegment(sketch, "E243", {"start": v(78.46, 67.5) * mm, "end": v(-146.08, 67.5) * mm});
            skLineSegment(sketch, "E244", {"start": v(-146.08, 67.5) * mm, "end": v(-156.08, 77.5) * mm});
            skLineSegment(sketch, "E245", {"start": v(-156.08, 77.5) * mm, "end": v(-218.08, 77.5) * mm});
            skLineSegment(sketch, "E246", {"start": v(-237.4, 62.68) * mm, "end": v(-256.2, -7.5) * mm});
            skArc(sketch, "E247", {"start": v(-243, -31.72) * mm, "mid": v(-39.94, -71.95) * mm, "end": v(166.94, -64.89) * mm});
            skLineSegment(sketch, "E248", {"start": v(168, 77.5) * mm, "end": v(168, 47.6) * mm, "construction": true});
            skLineSegment(sketch, "E249", {"start": v(-233.43, 77.5) * mm, "end": v(-233.43, 4.37) * mm, "construction": true});
            skPoint(sketch, "E250.visualSharp", {"position": v(186.33, -61.76) * mm});
            skArc(sketch, "E250.filletArc", {"start": v(166.94, -64.89) * mm, "mid": v(179.95, -57.14) * mm, "end": v(183.8, -42.5) * mm});
            skPoint(sketch, "E251.visualSharp", {"position": v(-261.08, -25.7) * mm});
            skArc(sketch, "E251.filletArc", {"start": v(-256.2, -7.5) * mm, "mid": v(-254.44, -22.25) * mm, "end": v(-243, -31.72) * mm});
            skPoint(sketch, "E252.visualSharp", {"position": v(168, 77.5) * mm});
            skArc(sketch, "E252.filletArc", {"start": v(170.29, 60.11) * mm, "mid": v(163.65, 72.54) * mm, "end": v(150.46, 77.5) * mm});
            skPoint(sketch, "E253.visualSharp", {"position": v(-233.43, 77.5) * mm});
            skArc(sketch, "E253.filletArc", {"start": v(-218.08, 77.5) * mm, "mid": v(-230.25, 73.37) * mm, "end": v(-237.4, 62.68) * mm});
            skLineSegment(sketch, "E254", {"start": v(166.94, -64.89) * mm, "end": v(164.4, -64.89) * mm, "construction": true});
            skLineSegment(sketch, "E255.0.0", {"start": v(-31, 34.5) * mm, "end": v(-3, 34.5) * mm});
            skLineSegment(sketch, "E255.0.1", {"start": v(-3, 34.5) * mm, "end": v(-3, 42.5) * mm});
            skLineSegment(sketch, "E255.0.2", {"start": v(-3, 42.5) * mm, "end": v(-31, 42.5) * mm});
            skLineSegment(sketch, "E255.0.3", {"start": v(-31, 42.5) * mm, "end": v(-31, 34.5) * mm});
            skLineSegment(sketch, "E255.1.0", {"start": v(-101, 34.5) * mm, "end": v(-81, 34.5) * mm});
            skLineSegment(sketch, "E255.1.1", {"start": v(-81, 34.5) * mm, "end": v(-81, 42.5) * mm});
            skLineSegment(sketch, "E255.1.2", {"start": v(-81, 42.5) * mm, "end": v(-101, 42.5) * mm});
            skLineSegment(sketch, "E255.1.3", {"start": v(-101, 42.5) * mm, "end": v(-101, 34.5) * mm});
            skLineSegment(sketch, "E255.2", {"start": v(-11, 34.5) * mm, "end": v(-11, 22.5) * mm});
            skLineSegment(sketch, "E255.3", {"start": v(-3, 34.5) * mm, "end": v(-3, 22.5) * mm});
            skLineSegment(sketch, "E255.4", {"start": v(-11, 22.5) * mm, "end": v(-3, 22.5) * mm});
            skLineSegment(sketch, "E255.5", {"start": v(-11, -42.5) * mm, "end": v(-11, -22.5) * mm});
            skLineSegment(sketch, "E255.6", {"start": v(-11, -42.5) * mm, "end": v(-3, -42.5) * mm});
            skLineSegment(sketch, "E255.7", {"start": v(-3, -42.5) * mm, "end": v(-3, -22.5) * mm});
            skLineSegment(sketch, "E255.8", {"start": v(-11, -22.5) * mm, "end": v(-3, -22.5) * mm});
            skCircle(sketch, "E256", {"center": v(103.46, 60.5) * mm, "radius": 15 * mm, "construction": true});
            skCircle(sketch, "E257", {"center": v(103.46, 60.5) * mm, "radius": 1.5 * mm});
            skLineSegment(sketch, "E258.bottom", {"start": v(43.46, 44) * mm, "end": v(63.46, 44) * mm, "construction": true});
            skLineSegment(sketch, "E258.top", {"start": v(43.46, 64) * mm, "end": v(63.46, 64) * mm, "construction": true});
            skLineSegment(sketch, "E258.left", {"start": v(43.46, 44) * mm, "end": v(43.46, 64) * mm, "construction": true});
            skLineSegment(sketch, "E258.right", {"start": v(63.46, 44) * mm, "end": v(63.46, 64) * mm, "construction": true});
            skPoint(sketch, "E258.middle", {"position": v(53.46, 54) * mm});
            skCircle(sketch, "E259", {"center": v(53.46, 54) * mm, "radius": 2.5 * mm});
            skCircle(sketch, "E260", {"center": v(-86, 60.5) * mm, "radius": 15 * mm, "construction": true});
            skCircle(sketch, "E261", {"center": v(-86, 60.5) * mm, "radius": 1.5 * mm});
            skCircle(sketch, "E262", {"center": v(-119.5, 42) * mm, "radius": 3 * mm});
            skCircle(sketch, "E263", {"center": v(-149.5, 42) * mm, "radius": 3 * mm});
            skLineSegment(sketch, "E264", {"start": v(-119.5, 42) * mm, "end": v(-149.5, 42) * mm, "construction": true});
            skPoint(sketch, "E265", {"position": v(-134.5, 42) * mm});
            skLineSegment(sketch, "E266.bottom", {"start": v(-107, 19.5) * mm, "end": v(-162, 19.5) * mm, "construction": true});
            skLineSegment(sketch, "E266.top", {"start": v(-107, 64.5) * mm, "end": v(-162, 64.5) * mm, "construction": true});
            skLineSegment(sketch, "E266.left", {"start": v(-107, 19.5) * mm, "end": v(-107, 64.5) * mm, "construction": true});
            skLineSegment(sketch, "E266.right", {"start": v(-162, 19.5) * mm, "end": v(-162, 64.5) * mm, "construction": true});
            skCircle(sketch, "E267.0.1.0", {"center": v(-119.5, 32) * mm, "radius": 3 * mm});
            skCircle(sketch, "E267.0.1.1", {"center": v(-149.5, 32) * mm, "radius": 3 * mm});
            skCircle(sketch, "E267.0.2.0", {"center": v(-119.5, 22) * mm, "radius": 3 * mm});
            skCircle(sketch, "E267.0.2.1", {"center": v(-149.5, 22) * mm, "radius": 3 * mm});
            skCircle(sketch, "E267.0.3.0", {"center": v(-119.5, 12) * mm, "radius": 3 * mm});
            skCircle(sketch, "E267.0.3.1", {"center": v(-149.5, 12) * mm, "radius": 3 * mm});
            skCircle(sketch, "E267.0.4.0", {"center": v(-119.5, 2) * mm, "radius": 3 * mm});
            skCircle(sketch, "E267.0.4.1", {"center": v(-149.5, 2) * mm, "radius": 3 * mm});
            skCircle(sketch, "E267.0.5.0", {"center": v(-119.5, -8) * mm, "radius": 3 * mm});
            skCircle(sketch, "E267.0.5.1", {"center": v(-149.5, -8) * mm, "radius": 3 * mm});
            skLineSegment(sketch, "E267.direction1", {"start": v(-149.5, 42) * mm, "end": v(-122.5, 42) * mm, "construction": true});
            skLineSegment(sketch, "E267.direction2", {"start": v(-149.5, 42) * mm, "end": v(-149.5, 32) * mm, "construction": true});
            skLineSegment(sketch, "E268", {"start": v(-119.5, -8) * mm, "end": v(-149.5, -8) * mm, "construction": true});
            skPoint(sketch, "E269", {"position": v(-134.5, -8) * mm});
            skLineSegment(sketch, "E270.bottom", {"start": v(-107, -30.5) * mm, "end": v(-162, -30.5) * mm, "construction": true});
            skLineSegment(sketch, "E270.top", {"start": v(-107, 14.5) * mm, "end": v(-162, 14.5) * mm, "construction": true});
            skLineSegment(sketch, "E270.left", {"start": v(-107, -30.5) * mm, "end": v(-107, 14.5) * mm, "construction": true});
            skLineSegment(sketch, "E270.right", {"start": v(-162, -30.5) * mm, "end": v(-162, 14.5) * mm, "construction": true});
            skLineSegment(sketch, "E271.bottom", {"start": v(-192, 56) * mm, "end": v(-172, 56) * mm, "construction": true});
            skLineSegment(sketch, "E271.top", {"start": v(-192, 76) * mm, "end": v(-172, 76) * mm, "construction": true});
            skLineSegment(sketch, "E271.left", {"start": v(-192, 56) * mm, "end": v(-192, 76) * mm, "construction": true});
            skLineSegment(sketch, "E271.right", {"start": v(-172, 56) * mm, "end": v(-172, 76) * mm, "construction": true});
            skPoint(sketch, "E271.middle", {"position": v(-182, 66) * mm});
            skCircle(sketch, "E272", {"center": v(-182, 66) * mm, "radius": 2.5 * mm});
            skPoint(sketch, "E273.0", {"position": v(-56, 34.5) * mm});
            skLineSegment(sketch, "E274", {"start": v(-56, 34.5) * mm, "end": v(-56, -55.5) * mm, "construction": true});
            skLineSegment(sketch, "E275.bottom", {"start": v(-18.5, -55.5) * mm, "end": v(-93.5, -55.5) * mm, "construction": true});
            skLineSegment(sketch, "E275.top", {"start": v(-18.5, -58.5) * mm, "end": v(-93.5, -58.5) * mm, "construction": true});
            skLineSegment(sketch, "E275.left", {"start": v(-18.5, -55.5) * mm, "end": v(-18.5, -58.5) * mm, "construction": true});
            skLineSegment(sketch, "E275.right", {"start": v(-93.5, -55.5) * mm, "end": v(-93.5, -58.5) * mm, "construction": true});
            skPoint(sketch, "E275.middle", {"position": v(-56, -57) * mm});
            skLineSegment(sketch, "E276.bottom", {"start": v(-107, -37) * mm, "end": v(-217, -37) * mm, "construction": true});
            skLineSegment(sketch, "E276.top", {"start": v(-107, -34) * mm, "end": v(-217, -34) * mm, "construction": true});
            skLineSegment(sketch, "E276.left", {"start": v(-107, -37) * mm, "end": v(-107, -34) * mm, "construction": true});
            skLineSegment(sketch, "E276.right", {"start": v(-217, -37) * mm, "end": v(-217, -34) * mm, "construction": true});
            skPoint(sketch, "E276.middle", {"position": v(-162, -35.5) * mm});
            skLineSegment(sketch, "E277.bottom", {"start": v(-26, -58.5) * mm, "end": v(-41, -58.5) * mm});
            skLineSegment(sketch, "E277.top", {"start": v(-26, -55.5) * mm, "end": v(-41, -55.5) * mm});
            skLineSegment(sketch, "E277.left", {"start": v(-26, -58.5) * mm, "end": v(-26, -55.5) * mm});
            skLineSegment(sketch, "E277.right", {"start": v(-41, -58.5) * mm, "end": v(-41, -55.5) * mm});
            skPoint(sketch, "E277.middle", {"position": v(-33.5, -57) * mm});
            skLineSegment(sketch, "E278.bottom", {"start": v(-78.5, -58.5) * mm, "end": v(-63.5, -58.5) * mm});
            skLineSegment(sketch, "E278.top", {"start": v(-78.5, -55.5) * mm, "end": v(-63.5, -55.5) * mm});
            skLineSegment(sketch, "E278.left", {"start": v(-78.5, -58.5) * mm, "end": v(-78.5, -55.5) * mm});
            skLineSegment(sketch, "E278.right", {"start": v(-63.5, -58.5) * mm, "end": v(-63.5, -55.5) * mm});
            skPoint(sketch, "E278.middle", {"position": v(-71, -57) * mm});
            skLineSegment(sketch, "E279.bottom", {"start": v(-122, -37) * mm, "end": v(-137, -37) * mm});
            skLineSegment(sketch, "E279.top", {"start": v(-122, -34) * mm, "end": v(-137, -34) * mm});
            skLineSegment(sketch, "E279.left", {"start": v(-122, -37) * mm, "end": v(-122, -34) * mm});
            skLineSegment(sketch, "E279.right", {"start": v(-137, -37) * mm, "end": v(-137, -34) * mm});
            skPoint(sketch, "E279.middle", {"position": v(-129.5, -35.5) * mm});
            skLineSegment(sketch, "E280.bottom", {"start": v(-194.5, -37) * mm, "end": v(-179.5, -37) * mm});
            skLineSegment(sketch, "E280.top", {"start": v(-194.5, -34) * mm, "end": v(-179.5, -34) * mm});
            skLineSegment(sketch, "E280.left", {"start": v(-194.5, -37) * mm, "end": v(-194.5, -34) * mm});
            skLineSegment(sketch, "E280.right", {"start": v(-179.5, -37) * mm, "end": v(-179.5, -34) * mm});
            skPoint(sketch, "E280.middle", {"position": v(-187, -35.5) * mm});
            skLineSegment(sketch, "E281.bottom", {"start": v(152, -42.5) * mm, "end": v(155, -42.5) * mm});
            skLineSegment(sketch, "E281.top", {"start": v(152, -27.5) * mm, "end": v(155, -27.5) * mm});
            skLineSegment(sketch, "E281.left", {"start": v(152, -42.5) * mm, "end": v(152, -27.5) * mm});
            skLineSegment(sketch, "E281.right", {"start": v(155, -42.5) * mm, "end": v(155, -27.5) * mm});
            skLineSegment(sketch, "E282.bottom", {"start": v(155, -7.5) * mm, "end": v(152, -7.5) * mm});
            skLineSegment(sketch, "E282.top", {"start": v(155, 7.5) * mm, "end": v(152, 7.5) * mm});
            skLineSegment(sketch, "E282.left", {"start": v(155, -7.5) * mm, "end": v(155, 7.5) * mm});
            skLineSegment(sketch, "E282.right", {"start": v(152, -7.5) * mm, "end": v(152, 7.5) * mm});
            skLineSegment(sketch, "E283.bottom", {"start": v(155, 27.5) * mm, "end": v(152, 27.5) * mm});
            skLineSegment(sketch, "E283.top", {"start": v(155, 42.5) * mm, "end": v(152, 42.5) * mm});
            skLineSegment(sketch, "E283.left", {"start": v(155, 27.5) * mm, "end": v(155, 42.5) * mm});
            skLineSegment(sketch, "E283.right", {"start": v(152, 27.5) * mm, "end": v(152, 42.5) * mm});
            skPoint(sketch, "E284", {"position": v(152, 0) * mm});
            skLineSegment(sketch, "E285.0", {"start": v(155.5, -43) * mm, "end": v(155.5, -27) * mm});
            skLineSegment(sketch, "E285.1", {"start": v(151.5, -43) * mm, "end": v(155.5, -43) * mm});
            skLineSegment(sketch, "E285.2", {"start": v(151.5, -43) * mm, "end": v(151.5, -27) * mm});
            skLineSegment(sketch, "E285.3", {"start": v(151.5, -27) * mm, "end": v(155.5, -27) * mm});
            skLineSegment(sketch, "E286.0", {"start": v(155.5, -8) * mm, "end": v(151.5, -8) * mm});
            skLineSegment(sketch, "E286.1", {"start": v(155.5, -8) * mm, "end": v(155.5, 8) * mm});
            skLineSegment(sketch, "E286.2", {"start": v(155.5, 8) * mm, "end": v(151.5, 8) * mm});
            skLineSegment(sketch, "E286.3", {"start": v(151.5, -8) * mm, "end": v(151.5, 8) * mm});
            skLineSegment(sketch, "E287.0", {"start": v(155.5, 27) * mm, "end": v(151.5, 27) * mm});
            skLineSegment(sketch, "E287.1", {"start": v(155.5, 27) * mm, "end": v(155.5, 43) * mm});
            skLineSegment(sketch, "E287.2", {"start": v(155.5, 43) * mm, "end": v(151.5, 43) * mm});
            skLineSegment(sketch, "E287.3", {"start": v(151.5, 27) * mm, "end": v(151.5, 43) * mm});
            skCircle(sketch, "E288", {"center": v(53.46, -57.5) * mm, "radius": 2.5 * mm});
            skLineSegment(sketch, "E289.bottom", {"start": v(43.46, -67.5) * mm, "end": v(63.46, -67.5) * mm, "construction": true});
            skLineSegment(sketch, "E289.top", {"start": v(43.46, -47.5) * mm, "end": v(63.46, -47.5) * mm, "construction": true});
            skLineSegment(sketch, "E289.left", {"start": v(43.46, -67.5) * mm, "end": v(43.46, -47.5) * mm, "construction": true});
            skLineSegment(sketch, "E289.right", {"start": v(63.46, -67.5) * mm, "end": v(63.46, -47.5) * mm, "construction": true});
            skSolve(sketch);
        }
        {
            var Q0;
            Q0 = qSketchRegion(id + "F26", true);
            extrude(context, id + "F27", {"entities" : qUnion([Q0]), "depth" : 8 * mm});
        }
        {
            var Q0;
            Q0=makeQuery(id+"F27.opExtrude","CAP_FACE",FACE,{"disambiguationData":[OSD([sQuery(id+"F26.wireOp",EDGE,"E240"),sQuery(id+"F26.wireOp",EDGE,"E241"),sQuery(id+"F26.wireOp",EDGE,"E242"),sQuery(id+"F26.wireOp",EDGE,"E243"),sQuery(id+"F26.wireOp",EDGE,"E244"),sQuery(id+"F26.wireOp",EDGE,"E245"),sQuery(id+"F26.wireOp",EDGE,"E246"),sQuery(id+"F26.wireOp",EDGE,"E247"),sQuery(id+"F26.wireOp",EDGE,"E250.filletArc"),sQuery(id+"F26.wireOp",EDGE,"E251.filletArc"),sQuery(id+"F26.wireOp",EDGE,"E252.filletArc"),sQuery(id+"F26.wireOp",EDGE,"E253.filletArc"),sQuery(id+"F26.wireOp",EDGE,"E255.0.0"),sQuery(id+"F26.wireOp",EDGE,"E255.0.1"),sQuery(id+"F26.wireOp",EDGE,"E255.0.2"),sQuery(id+"F26.wireOp",EDGE,"E255.0.3"),sQuery(id+"F26.wireOp",EDGE,"E255.1.0"),sQuery(id+"F26.wireOp",EDGE,"E255.1.1"),sQuery(id+"F26.wireOp",EDGE,"E255.1.2"),sQuery(id+"F26.wireOp",EDGE,"E255.1.3"),sQuery(id+"F26.wireOp",EDGE,"E255.2"),sQuery(id+"F26.wireOp",EDGE,"E255.3"),sQuery(id+"F26.wireOp",EDGE,"E255.4"),sQuery(id+"F26.wireOp",EDGE,"E255.5"),sQuery(id+"F26.wireOp",EDGE,"E255.6"),sQuery(id+"F26.wireOp",EDGE,"E255.7"),sQuery(id+"F26.wireOp",EDGE,"E255.8"),sQuery(id+"F26.wireOp",EDGE,"20cfc65d-f90a-426b-b5b5-0eab701f50cc.0"),sQuery(id+"F26.wireOp",EDGE,"20cfc65d-f90a-426b-b5b5-0eab701f50cc.1"),sQuery(id+"F26.wireOp",EDGE,"20cfc65d-f90a-426b-b5b5-0eab701f50cc.2"),sQuery(id+"F26.wireOp",EDGE,"20cfc65d-f90a-426b-b5b5-0eab701f50cc.3"),sQuery(id+"F26.wireOp",EDGE,"2a59b45d-29ad-4de5-82b8-f507ae6de48c.0"),sQuery(id+"F26.wireOp",EDGE,"2a59b45d-29ad-4de5-82b8-f507ae6de48c.1"),sQuery(id+"F26.wireOp",EDGE,"2a59b45d-29ad-4de5-82b8-f507ae6de48c.2"),sQuery(id+"F26.wireOp",EDGE,"2a59b45d-29ad-4de5-82b8-f507ae6de48c.3"),sQuery(id+"F26.wireOp",EDGE,"f9551b3c-63d4-4721-b57d-519848da493c.0"),sQuery(id+"F26.wireOp",EDGE,"f9551b3c-63d4-4721-b57d-519848da493c.1"),sQuery(id+"F26.wireOp",EDGE,"f9551b3c-63d4-4721-b57d-519848da493c.2"),sQuery(id+"F26.wireOp",EDGE,"f9551b3c-63d4-4721-b57d-519848da493c.3"),sQuery(id+"F26.wireOp",EDGE,"E257"),sQuery(id+"F26.wireOp",EDGE,"E259"),sQuery(id+"F26.wireOp",EDGE,"E261"),sQuery(id+"F26.wireOp",EDGE,"E262"),sQuery(id+"F26.wireOp",EDGE,"E263"),sQuery(id+"F26.wireOp",EDGE,"E267.0.1.0"),sQuery(id+"F26.wireOp",EDGE,"E267.0.1.1"),sQuery(id+"F26.wireOp",EDGE,"E267.0.2.0"),sQuery(id+"F26.wireOp",EDGE,"E267.0.2.1"),sQuery(id+"F26.wireOp",EDGE,"E267.0.3.0"),sQuery(id+"F26.wireOp",EDGE,"E267.0.3.1"),sQuery(id+"F26.wireOp",EDGE,"E267.0.4.0"),sQuery(id+"F26.wireOp",EDGE,"E267.0.4.1"),sQuery(id+"F26.wireOp",EDGE,"E267.0.5.0"),sQuery(id+"F26.wireOp",EDGE,"E267.0.5.1"),sQuery(id+"F26.wireOp",EDGE,"E272"),sQuery(id+"F26.wireOp",EDGE,"E277.bottom"),sQuery(id+"F26.wireOp",EDGE,"E277.top"),sQuery(id+"F26.wireOp",EDGE,"E277.left"),sQuery(id+"F26.wireOp",EDGE,"E277.right"),sQuery(id+"F26.wireOp",EDGE,"E278.bottom"),sQuery(id+"F26.wireOp",EDGE,"E278.top"),sQuery(id+"F26.wireOp",EDGE,"E278.left"),sQuery(id+"F26.wireOp",EDGE,"E278.right"),sQuery(id+"F26.wireOp",EDGE,"E279.bottom"),sQuery(id+"F26.wireOp",EDGE,"E279.top"),sQuery(id+"F26.wireOp",EDGE,"E279.left"),sQuery(id+"F26.wireOp",EDGE,"E279.right"),sQuery(id+"F26.wireOp",EDGE,"E280.bottom"),sQuery(id+"F26.wireOp",EDGE,"E280.top"),sQuery(id+"F26.wireOp",EDGE,"E280.left"),sQuery(id+"F26.wireOp",EDGE,"E280.right")])],"isStart":false});
            var sketch = newSketch(context, id + "F28", { "sketchPlane" : qUnion([Q0])});
            skLineSegment(sketch, "E290.bottom", {"start": v(-21, -42.5) * mm, "end": v(-21, -42.5) * mm});
            skLineSegment(sketch, "E290.top", {"start": v(-21, 24.5) * mm, "end": v(-101, 24.5) * mm});
            skLineSegment(sketch, "E290.left", {"start": v(-21, -42.5) * mm, "end": v(-21, 24.5) * mm});
            skLineSegment(sketch, "E290.right", {"start": v(-101, -42.5) * mm, "end": v(-101, 24.5) * mm});
            skLineSegment(sketch, "E291", {"start": v(-21, 24.5) * mm, "end": v(-44, -42.5) * mm});
            skLineSegment(sketch, "E292", {"start": v(-101, 24.5) * mm, "end": v(-78, -42.5) * mm});
            skLineSegment(sketch, "E293", {"start": v(-44, -42.5) * mm, "end": v(-44, -42.5) * mm});
            skLineSegment(sketch, "E294", {"start": v(-21, -42.5) * mm, "end": v(-44, -42.5) * mm});
            skLineSegment(sketch, "E295", {"start": v(-78, -42.5) * mm, "end": v(-101, -42.5) * mm});
            skLineSegment(sketch, "E296", {"start": v(-78, -42.5) * mm, "end": v(-78, -42.5) * mm});
            skLineSegment(sketch, "E297", {"start": v(-44, -42.5) * mm, "end": v(-78, -42.5) * mm});
            skLineSegment(sketch, "E298.0", {"start": v(-28.91, 16.85) * mm, "end": v(-47.1, -36.15) * mm});
            skLineSegment(sketch, "E298.1", {"start": v(-30.8, 19.5) * mm, "end": v(-91.2, 19.5) * mm});
            skLineSegment(sketch, "E298.2", {"start": v(-93.09, 16.85) * mm, "end": v(-74.9, -36.15) * mm});
            skLineSegment(sketch, "E298.3", {"start": v(-49, -37.5) * mm, "end": v(-73, -37.5) * mm});
            skLineSegment(sketch, "E299.MirrorCS", {"start": v(-21, -42.5) * mm, "end": v(-21, -109.5) * mm});
            skLineSegment(sketch, "E300.0", {"start": v(-25, -40.5) * mm, "end": v(-38.4, -40.5) * mm});
            skLineSegment(sketch, "E300.1", {"start": v(-23, -38.5) * mm, "end": v(-23, 0.53) * mm});
            skLineSegment(sketch, "E300.2", {"start": v(-26.9, 1.18) * mm, "end": v(-40.29, -37.85) * mm});
            skLineSegment(sketch, "E301.0", {"start": v(-83.6, -40.5) * mm, "end": v(-97, -40.5) * mm});
            skLineSegment(sketch, "E301.1", {"start": v(-95.1, 1.18) * mm, "end": v(-81.71, -37.85) * mm});
            skLineSegment(sketch, "E301.2", {"start": v(-99, -38.5) * mm, "end": v(-99, 0.53) * mm});
            skPoint(sketch, "E302.visualSharp", {"position": v(-41.2, -40.5) * mm});
            skArc(sketch, "E302.filletArc", {"start": v(-40.29, -37.85) * mm, "mid": v(-40.03, -39.66) * mm, "end": v(-38.4, -40.5) * mm});
            skPoint(sketch, "E303.visualSharp", {"position": v(-23, -40.5) * mm});
            skArc(sketch, "E303.filletArc", {"start": v(-25, -40.5) * mm, "mid": v(-23.59, -39.91) * mm, "end": v(-23, -38.5) * mm});
            skPoint(sketch, "E304.visualSharp", {"position": v(-23, 12.51) * mm});
            skArc(sketch, "E304.filletArc", {"start": v(-23, 0.53) * mm, "mid": v(-24.67, 2.5) * mm, "end": v(-26.9, 1.18) * mm});
            skPoint(sketch, "E305.visualSharp", {"position": v(-47.57, -37.5) * mm});
            skArc(sketch, "E305.filletArc", {"start": v(-49, -37.5) * mm, "mid": v(-47.84, -37.13) * mm, "end": v(-47.1, -36.15) * mm});
            skPoint(sketch, "E306.visualSharp", {"position": v(-28, 19.5) * mm});
            skArc(sketch, "E306.filletArc", {"start": v(-28.91, 16.85) * mm, "mid": v(-29.18, 18.66) * mm, "end": v(-30.8, 19.5) * mm});
            skPoint(sketch, "E307.visualSharp", {"position": v(-94, 19.5) * mm});
            skArc(sketch, "E307.filletArc", {"start": v(-91.2, 19.5) * mm, "mid": v(-92.82, 18.66) * mm, "end": v(-93.09, 16.85) * mm});
            skPoint(sketch, "E308.visualSharp", {"position": v(-74.43, -37.5) * mm});
            skArc(sketch, "E308.filletArc", {"start": v(-74.9, -36.15) * mm, "mid": v(-74.16, -37.13) * mm, "end": v(-73, -37.5) * mm});
            skPoint(sketch, "E309.visualSharp", {"position": v(-80.8, -40.5) * mm});
            skArc(sketch, "E309.filletArc", {"start": v(-83.6, -40.5) * mm, "mid": v(-81.97, -39.66) * mm, "end": v(-81.71, -37.85) * mm});
            skPoint(sketch, "E310.visualSharp", {"position": v(-99, -40.5) * mm});
            skArc(sketch, "E310.filletArc", {"start": v(-99, -38.5) * mm, "mid": v(-98.41, -39.91) * mm, "end": v(-97, -40.5) * mm});
            skPoint(sketch, "E311.visualSharp", {"position": v(-99, 12.51) * mm});
            skArc(sketch, "E311.filletArc", {"start": v(-95.1, 1.18) * mm, "mid": v(-97.33, 2.5) * mm, "end": v(-99, 0.53) * mm});
            skSolve(sketch);
        }
        {
            var Q0;
            Q0=makeQuery(id+"F28.imprint","IMPRINT",FACE,{"disambiguationData":[TD([[makeQuery(id+"F28.imprint","IMPRINT",EDGE,{"derivedFrom":sQuery(id+"F28.wireOp",EDGE,"E300.0")}),-1.0]])]});
            var Q1;
            Q1=makeQuery(id+"F28.imprint","IMPRINT",FACE,{"disambiguationData":[TD([[makeQuery(id+"F28.imprint","IMPRINT",EDGE,{"derivedFrom":sQuery(id+"F28.wireOp",EDGE,"E298.0")}),-1.0]])]});
            var Q2;
            Q2=makeQuery(id+"F28.imprint","IMPRINT",FACE,{"disambiguationData":[TD([[makeQuery(id+"F28.imprint","IMPRINT",EDGE,{"derivedFrom":sQuery(id+"F28.wireOp",EDGE,"E301.0")}),-1.0]])]});
            extrude(context, id + "F29", {"entities" : qUnion([Q0, Q1, Q2]), "operationType" : NewBodyOperationType.REMOVE, "oppositeDirection" : true, "depth" : 25 * mm});
        }
    });
